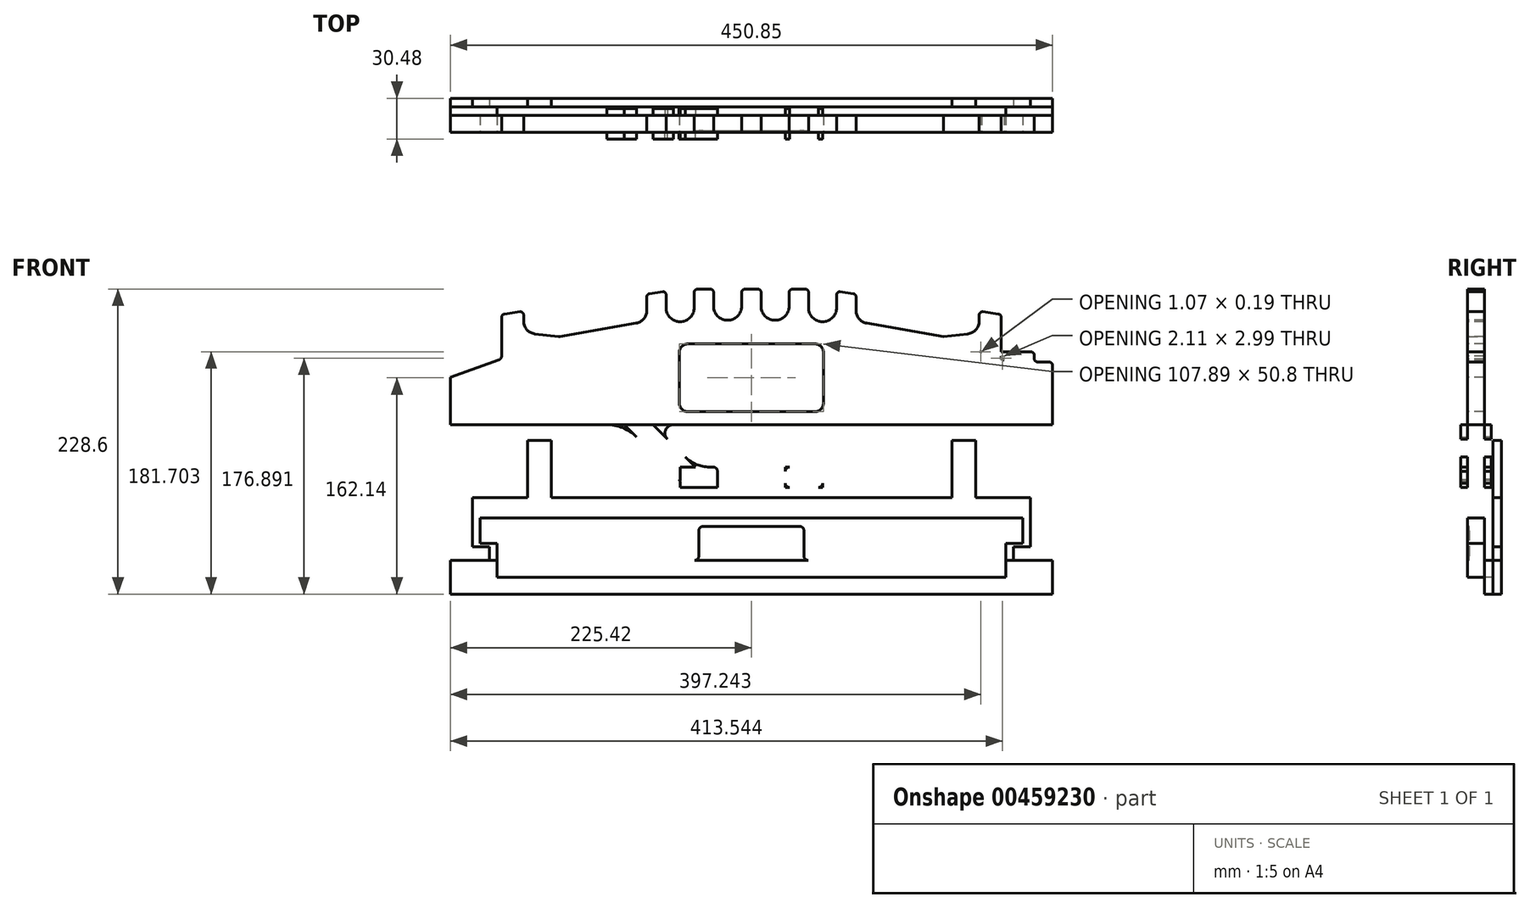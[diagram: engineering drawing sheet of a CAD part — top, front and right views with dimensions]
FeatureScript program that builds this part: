
annotation { "Feature Type Name" : "Feature", "Feature Type Description" : "" }
export const myFeature = defineFeature(function(context is Context, id is Id, definition is map)
    precondition{}
    {
        {
            var Q0;
            Q0=qCreatedBy(makeId("Front.planeOp"),FACE);
            var sketch = newSketch(context, id + "F0", { "sketchPlane" : qUnion([Q0])});
            skLineSegment(sketch, "E0", {"start": v(225.43, 44.45) * mm, "end": v(225.43, -101.6) * mm});
            skArc(sketch, "E1", {"start": v(225.42, 44.45) * mm, "mid": v(224.68, 46.25) * mm, "end": v(222.88, 47) * mm});
            skLineSegment(sketch, "E2", {"start": v(214.35, 47) * mm, "end": v(222.88, 47) * mm});
            skArc(sketch, "E3", {"start": v(211.8, 49.53) * mm, "mid": v(212.55, 47.73) * mm, "end": v(214.35, 47) * mm});
            skLineSegment(sketch, "E4", {"start": v(211.8, 52.07) * mm, "end": v(211.8, 49.53) * mm});
            skArc(sketch, "E5", {"start": v(211.8, 52.07) * mm, "mid": v(211.06, 53.87) * mm, "end": v(209.27, 54.6) * mm});
            skLineSegment(sketch, "E6", {"start": v(171.8, 54.61) * mm, "end": v(209.27, 54.61) * mm});
            skArc(sketch, "E7", {"start": v(187.07, 57.15) * mm, "mid": v(187.81, 55.35) * mm, "end": v(189.61, 54.61) * mm});
            skLineSegment(sketch, "E8", {"start": v(187.07, 80.43) * mm, "end": v(187.07, 57.15) * mm});
            skArc(sketch, "E9", {"start": v(187.07, 80.43) * mm, "mid": v(186.45, 82.1) * mm, "end": v(184.9, 82.94) * mm});
            skLineSegment(sketch, "E10", {"start": v(173.46, 84.58) * mm, "end": v(184.9, 82.94) * mm});
            skArc(sketch, "E11", {"start": v(173.46, 84.58) * mm, "mid": v(171.44, 83.98) * mm, "end": v(170.56, 82.06) * mm});
            skLineSegment(sketch, "E12", {"start": v(170.56, 77.52) * mm, "end": v(170.56, 82.06) * mm});
            skArc(sketch, "E13", {"start": v(162.11, 68.05) * mm, "mid": v(168.14, 71.17) * mm, "end": v(170.56, 77.52) * mm});
            skLineSegment(sketch, "E14", {"start": v(143.97, 65.99) * mm, "end": v(162.11, 68.05) * mm});
            skArc(sketch, "E15", {"start": v(141.12, 66.32) * mm, "mid": v(142.53, 65.99) * mm, "end": v(143.97, 65.99) * mm});
            skLineSegment(sketch, "E16", {"start": v(122.27, 73.06) * mm, "end": v(141.12, 66.32) * mm});
            skArc(sketch, "E17", {"start": v(115.95, 82.03) * mm, "mid": v(117.69, 76.54) * mm, "end": v(122.27, 73.06) * mm});
            skLineSegment(sketch, "E18", {"start": v(115.95, 90.6) * mm, "end": v(115.95, 82.03) * mm});
            skArc(sketch, "E19", {"start": v(115.95, 90.6) * mm, "mid": v(115.33, 92.26) * mm, "end": v(113.77, 93.1) * mm});
            skLineSegment(sketch, "E20", {"start": v(102.34, 94.74) * mm, "end": v(113.77, 93.1) * mm});
            skArc(sketch, "E21", {"start": v(102.34, 94.74) * mm, "mid": v(100.32, 94.14) * mm, "end": v(99.44, 92.22) * mm});
            skLineSegment(sketch, "E22", {"start": v(99.44, 85.4) * mm, "end": v(99.44, 92.22) * mm});
            skArc(sketch, "E23", {"start": v(80.4, 85.4) * mm, "mid": v(89.92, 75.87) * mm, "end": v(99.44, 85.4) * mm});
            skLineSegment(sketch, "E24", {"start": v(80.4, 95.67) * mm, "end": v(80.4, 85.4) * mm});
            skArc(sketch, "E25", {"start": v(80.4, 95.67) * mm, "mid": v(79.77, 97.34) * mm, "end": v(78.21, 98.19) * mm});
            skLineSegment(sketch, "E26", {"start": v(66.78, 99.82) * mm, "end": v(78.21, 98.19) * mm});
            skArc(sketch, "E27", {"start": v(66.78, 99.82) * mm, "mid": v(64.76, 99.22) * mm, "end": v(63.88, 97.3) * mm});
            skLineSegment(sketch, "E28", {"start": v(63.88, 87.64) * mm, "end": v(63.88, 97.3) * mm});
            skArc(sketch, "E29", {"start": v(44.83, 87.64) * mm, "mid": v(54.36, 78.12) * mm, "end": v(63.88, 87.64) * mm});
            skLineSegment(sketch, "E30", {"start": v(44.83, 99.06) * mm, "end": v(44.83, 87.64) * mm});
            skArc(sketch, "E31", {"start": v(44.83, 99.06) * mm, "mid": v(44.09, 100.86) * mm, "end": v(42.3, 101.6) * mm});
            skLineSegment(sketch, "E32", {"start": v(30.86, 101.6) * mm, "end": v(42.3, 101.6) * mm});
            skArc(sketch, "E33", {"start": v(30.86, 101.6) * mm, "mid": v(29.06, 100.86) * mm, "end": v(28.32, 99.06) * mm});
            skLineSegment(sketch, "E34", {"start": v(28.32, 88.76) * mm, "end": v(28.32, 99.06) * mm});
            skArc(sketch, "E35", {"start": v(9.27, 88.76) * mm, "mid": v(18.8, 79.24) * mm, "end": v(28.32, 88.76) * mm});
            skLineSegment(sketch, "E36", {"start": v(9.27, 99.06) * mm, "end": v(9.27, 88.76) * mm});
            skArc(sketch, "E37", {"start": v(9.27, 99.06) * mm, "mid": v(8.53, 100.86) * mm, "end": v(6.73, 101.6) * mm});
            skLineSegment(sketch, "E38", {"start": v(-4.7, 101.6) * mm, "end": v(6.73, 101.6) * mm});
            skArc(sketch, "E39", {"start": v(-4.7, 101.6) * mm, "mid": v(-6.5, 100.86) * mm, "end": v(-7.24, 99.06) * mm});
            skLineSegment(sketch, "E40", {"start": v(-7.24, 88.76) * mm, "end": v(-7.24, 99.06) * mm});
            skArc(sketch, "E41", {"start": v(-26.29, 88.76) * mm, "mid": v(-16.76, 79.24) * mm, "end": v(-7.24, 88.76) * mm});
            skLineSegment(sketch, "E42", {"start": v(-26.29, 99.06) * mm, "end": v(-26.29, 88.76) * mm});
            skArc(sketch, "E43", {"start": v(-26.29, 99.06) * mm, "mid": v(-27.03, 100.86) * mm, "end": v(-28.83, 101.6) * mm});
            skLineSegment(sketch, "E44", {"start": v(-40.26, 101.6) * mm, "end": v(-28.83, 101.6) * mm});
            skArc(sketch, "E45", {"start": v(-40.26, 101.6) * mm, "mid": v(-42.06, 100.86) * mm, "end": v(-42.8, 99.06) * mm});
            skLineSegment(sketch, "E46", {"start": v(-42.8, 87.64) * mm, "end": v(-42.8, 99.06) * mm});
            skArc(sketch, "E47", {"start": v(-61.85, 87.64) * mm, "mid": v(-52.32, 78.12) * mm, "end": v(-42.8, 87.64) * mm});
            skLineSegment(sketch, "E48", {"start": v(-61.85, 97.3) * mm, "end": v(-61.85, 87.64) * mm});
            skArc(sketch, "E49", {"start": v(-61.85, 97.3) * mm, "mid": v(-62.72, 99.23) * mm, "end": v(-64.75, 99.82) * mm});
            skLineSegment(sketch, "E50", {"start": v(-76.18, 98.19) * mm, "end": v(-64.75, 99.82) * mm});
            skArc(sketch, "E51", {"start": v(-76.18, 98.19) * mm, "mid": v(-77.74, 97.34) * mm, "end": v(-78.36, 95.67) * mm});
            skLineSegment(sketch, "E52", {"start": v(-78.36, 85.4) * mm, "end": v(-78.36, 95.67) * mm});
            skArc(sketch, "E53", {"start": v(-97.4, 85.4) * mm, "mid": v(-87.88, 75.87) * mm, "end": v(-78.36, 85.4) * mm});
            skLineSegment(sketch, "E54", {"start": v(-97.4, 92.23) * mm, "end": v(-97.4, 85.4) * mm});
            skArc(sketch, "E55", {"start": v(-97.4, 92.23) * mm, "mid": v(-98.28, 94.15) * mm, "end": v(-100.3, 94.74) * mm});
            skLineSegment(sketch, "E56", {"start": v(-111.74, 93.1) * mm, "end": v(-100.3, 94.74) * mm});
            skArc(sketch, "E57", {"start": v(-111.74, 93.1) * mm, "mid": v(-113.3, 92.26) * mm, "end": v(-113.92, 90.6) * mm});
            skLineSegment(sketch, "E58", {"start": v(-113.92, 82.03) * mm, "end": v(-113.92, 90.6) * mm});
            skArc(sketch, "E59", {"start": v(-120.24, 73.06) * mm, "mid": v(-115.66, 76.54) * mm, "end": v(-113.92, 82.03) * mm});
            skLineSegment(sketch, "E60", {"start": v(-139.09, 66.32) * mm, "end": v(-120.24, 73.06) * mm});
            skArc(sketch, "E61", {"start": v(-140.8, 65.96) * mm, "mid": v(-139.93, 66.08) * mm, "end": v(-139.09, 66.32) * mm});
            skLineSegment(sketch, "E62", {"start": v(-193.92, 62.35) * mm, "end": v(-140.8, 65.96) * mm});
            skArc(sketch, "E63", {"start": v(-204.09, 71.85) * mm, "mid": v(-201.07, 64.9) * mm, "end": v(-193.92, 62.35) * mm});
            skLineSegment(sketch, "E64", {"start": v(-204.09, 78.74) * mm, "end": v(-204.09, 71.85) * mm});
            skArc(sketch, "E65", {"start": v(-204.09, 78.74) * mm, "mid": v(-204.83, 80.54) * mm, "end": v(-206.63, 81.28) * mm});
            skLineSegment(sketch, "E66", {"start": v(-222.89, 81.28) * mm, "end": v(-206.63, 81.28) * mm});
            skArc(sketch, "E67", {"start": v(-222.89, 81.28) * mm, "mid": v(-224.68, 80.54) * mm, "end": v(-225.43, 78.74) * mm});
            skLineSegment(sketch, "E68", {"start": v(-225.43, -101.6) * mm, "end": v(-225.43, 78.74) * mm});
            skLineSegment(sketch, "E69", {"start": v(-193.68, -101.6) * mm, "end": v(-225.43, -101.6) * mm});
            skLineSegment(sketch, "E70", {"start": v(-193.68, -88.9) * mm, "end": v(-193.68, -101.6) * mm});
            skLineSegment(sketch, "E71", {"start": v(-206.38, -88.9) * mm, "end": v(-193.68, -88.9) * mm});
            skLineSegment(sketch, "E72", {"start": v(-206.38, -57.15) * mm, "end": v(-206.38, -88.9) * mm});
            skLineSegment(sketch, "E73", {"start": v(-165.35, -57.15) * mm, "end": v(-206.38, -57.15) * mm});
            skLineSegment(sketch, "E74", {"start": v(-165.35, -14.48) * mm, "end": v(-165.35, -57.15) * mm});
            skLineSegment(sketch, "E75", {"start": v(-152.4, -14.48) * mm, "end": v(-165.35, -14.48) * mm});
            skLineSegment(sketch, "E76", {"start": v(-152.4, -57.15) * mm, "end": v(-152.4, -14.48) * mm});
            skLineSegment(sketch, "E77", {"start": v(152.4, -57.15) * mm, "end": v(-152.4, -57.15) * mm});
            skLineSegment(sketch, "E78", {"start": v(152.4, -14.48) * mm, "end": v(152.4, -57.15) * mm});
            skLineSegment(sketch, "E79", {"start": v(165.35, -14.48) * mm, "end": v(152.4, -14.48) * mm});
            skLineSegment(sketch, "E80", {"start": v(165.35, -57.15) * mm, "end": v(165.35, -14.48) * mm});
            skLineSegment(sketch, "E81", {"start": v(206.38, -57.15) * mm, "end": v(165.35, -57.15) * mm});
            skLineSegment(sketch, "E82", {"start": v(206.38, -88.9) * mm, "end": v(206.38, -57.15) * mm});
            skLineSegment(sketch, "E83", {"start": v(193.68, -88.9) * mm, "end": v(206.38, -88.9) * mm});
            skLineSegment(sketch, "E84", {"start": v(193.68, -101.6) * mm, "end": v(193.68, -88.9) * mm});
            skLineSegment(sketch, "E85", {"start": v(225.43, -101.6) * mm, "end": v(193.68, -101.6) * mm});
            skLineSegment(sketch, "E86", {"start": v(47.6, 9.74) * mm, "end": v(-47.6, 9.74) * mm});
            skArc(sketch, "E87", {"start": v(-53.95, 16.1) * mm, "mid": v(-52.09, 11.6) * mm, "end": v(-47.6, 9.74) * mm});
            skLineSegment(sketch, "E88", {"start": v(-53.95, 16.1) * mm, "end": v(-53.95, 54.2) * mm});
            skArc(sketch, "E89", {"start": v(-47.6, 60.54) * mm, "mid": v(-52.09, 58.68) * mm, "end": v(-53.95, 54.2) * mm});
            skLineSegment(sketch, "E90", {"start": v(-47.6, 60.54) * mm, "end": v(47.6, 60.54) * mm});
            skArc(sketch, "E91", {"start": v(53.95, 54.2) * mm, "mid": v(52.09, 58.68) * mm, "end": v(47.6, 60.54) * mm});
            skLineSegment(sketch, "E92", {"start": v(53.95, 54.2) * mm, "end": v(53.95, 16.1) * mm});
            skArc(sketch, "E93", {"start": v(47.6, 9.74) * mm, "mid": v(52.09, 11.6) * mm, "end": v(53.95, 16.1) * mm});
            skLineSegment(sketch, "E94", {"start": v(225.43, -101.6) * mm, "end": v(-225.43, -101.6) * mm, "construction": true});
            skLineSegment(sketch, "E95", {"start": v(-225.43, -101.6) * mm, "end": v(-225.43, 0) * mm, "construction": true});
            skLineSegment(sketch, "E96", {"start": v(-225.43, 0) * mm, "end": v(225.43, 0) * mm});
            skLineSegment(sketch, "E97", {"start": v(225.43, 0) * mm, "end": v(225.43, -101.6) * mm, "construction": true});
            skLineSegment(sketch, "E98", {"start": v(0, -604.73) * mm, "end": v(0, 474.28) * mm, "construction": true});
            skArc(sketch, "E99.MirrorCS", {"start": v(-44.83, 99.06) * mm, "mid": v(-44.09, 100.86) * mm, "end": v(-42.3, 101.6) * mm});
            skArc(sketch, "E100.MirrorCS", {"start": v(111.74, 93.1) * mm, "mid": v(113.3, 92.26) * mm, "end": v(113.92, 90.6) * mm});
            skLineSegment(sketch, "E101.MirrorCS", {"start": v(7.24, 88.76) * mm, "end": v(7.24, 99.06) * mm});
            skLineSegment(sketch, "E102.MirrorCS", {"start": v(-30.86, 101.6) * mm, "end": v(-42.3, 101.6) * mm});
            skArc(sketch, "E103.MirrorCS", {"start": v(4.7, 101.6) * mm, "mid": v(6.5, 100.86) * mm, "end": v(7.24, 99.06) * mm});
            skArc(sketch, "E104.MirrorCS", {"start": v(-211.8, 52.07) * mm, "mid": v(-211.06, 53.87) * mm, "end": v(-209.27, 54.6) * mm});
            skLineSegment(sketch, "E105.MirrorCS", {"start": v(-211.8, 52.07) * mm, "end": v(-211.8, 49.53) * mm});
            skArc(sketch, "E106.MirrorCS", {"start": v(-211.8, 49.53) * mm, "mid": v(-212.55, 47.73) * mm, "end": v(-214.35, 47) * mm});
            skLineSegment(sketch, "E107.MirrorCS", {"start": v(113.92, 82.03) * mm, "end": v(113.92, 90.6) * mm});
            skLineSegment(sketch, "E108.MirrorCS", {"start": v(-28.32, 88.76) * mm, "end": v(-28.32, 99.06) * mm});
            skLineSegment(sketch, "E109.MirrorCS", {"start": v(-115.95, 90.6) * mm, "end": v(-115.95, 82.03) * mm});
            skLineSegment(sketch, "E110.MirrorCS", {"start": v(4.7, 101.6) * mm, "end": v(-6.73, 101.6) * mm});
            skArc(sketch, "E111.MirrorCS", {"start": v(-30.86, 101.6) * mm, "mid": v(-29.06, 100.86) * mm, "end": v(-28.32, 99.06) * mm});
            skArc(sketch, "E112.MirrorCS", {"start": v(-9.27, 99.06) * mm, "mid": v(-8.53, 100.86) * mm, "end": v(-6.73, 101.6) * mm});
            skLineSegment(sketch, "E113.MirrorCS", {"start": v(40.26, 101.6) * mm, "end": v(28.83, 101.6) * mm});
            skArc(sketch, "E114.MirrorCS", {"start": v(40.26, 101.6) * mm, "mid": v(42.06, 100.86) * mm, "end": v(42.8, 99.06) * mm});
            skLineSegment(sketch, "E115.MirrorCS", {"start": v(-9.27, 99.06) * mm, "end": v(-9.27, 88.76) * mm});
            skArc(sketch, "E116.MirrorCS", {"start": v(140.8, 65.96) * mm, "mid": v(139.93, 66.08) * mm, "end": v(139.09, 66.32) * mm});
            skLineSegment(sketch, "E117.MirrorCS", {"start": v(-102.34, 94.74) * mm, "end": v(-113.77, 93.1) * mm});
            skArc(sketch, "E118.MirrorCS", {"start": v(26.29, 99.06) * mm, "mid": v(27.03, 100.86) * mm, "end": v(28.83, 101.6) * mm});
            skArc(sketch, "E119.MirrorCS", {"start": v(76.18, 98.19) * mm, "mid": v(77.74, 97.34) * mm, "end": v(78.36, 95.67) * mm});
            skArc(sketch, "E120.MirrorCS", {"start": v(-115.95, 90.6) * mm, "mid": v(-115.33, 92.26) * mm, "end": v(-113.77, 93.1) * mm});
            skLineSegment(sketch, "E121.MirrorCS", {"start": v(26.29, 99.06) * mm, "end": v(26.29, 88.76) * mm});
            skLineSegment(sketch, "E122.MirrorCS", {"start": v(76.18, 98.19) * mm, "end": v(64.75, 99.82) * mm});
            skLineSegment(sketch, "E123.MirrorCS", {"start": v(97.4, 92.23) * mm, "end": v(97.4, 85.4) * mm});
            skLineSegment(sketch, "E124.MirrorCS", {"start": v(-99.44, 85.4) * mm, "end": v(-99.44, 92.22) * mm});
            skArc(sketch, "E125.MirrorCS", {"start": v(61.85, 97.3) * mm, "mid": v(62.72, 99.23) * mm, "end": v(64.75, 99.82) * mm});
            skArc(sketch, "E126.MirrorCS", {"start": v(204.09, 78.74) * mm, "mid": v(204.83, 80.54) * mm, "end": v(206.63, 81.28) * mm});
            skLineSegment(sketch, "E127.MirrorCS", {"start": v(42.8, 87.64) * mm, "end": v(42.8, 99.06) * mm});
            skArc(sketch, "E128.MirrorCS", {"start": v(-102.34, 94.74) * mm, "mid": v(-100.32, 94.14) * mm, "end": v(-99.44, 92.22) * mm});
            skLineSegment(sketch, "E129.MirrorCS", {"start": v(-63.88, 87.64) * mm, "end": v(-63.88, 97.3) * mm});
            skLineSegment(sketch, "E130.MirrorCS", {"start": v(111.74, 93.1) * mm, "end": v(100.3, 94.74) * mm});
            skLineSegment(sketch, "E131.MirrorCS", {"start": v(61.85, 97.3) * mm, "end": v(61.85, 87.64) * mm});
            skLineSegment(sketch, "E132.MirrorCS", {"start": v(204.09, 78.74) * mm, "end": v(204.09, 71.85) * mm});
            skLineSegment(sketch, "E133.MirrorCS", {"start": v(78.36, 85.4) * mm, "end": v(78.36, 95.67) * mm});
            skArc(sketch, "E134.MirrorCS", {"start": v(-66.78, 99.82) * mm, "mid": v(-64.76, 99.22) * mm, "end": v(-63.88, 97.3) * mm});
            skArc(sketch, "E135.MirrorCS", {"start": v(97.4, 92.23) * mm, "mid": v(98.28, 94.15) * mm, "end": v(100.3, 94.74) * mm});
            skLineSegment(sketch, "E136.MirrorCS", {"start": v(-170.56, 77.52) * mm, "end": v(-170.56, 82.06) * mm});
            skArc(sketch, "E137.MirrorCS", {"start": v(-173.46, 84.58) * mm, "mid": v(-171.44, 83.98) * mm, "end": v(-170.56, 82.06) * mm});
            skLineSegment(sketch, "E138.MirrorCS", {"start": v(-173.46, 84.58) * mm, "end": v(-184.9, 82.94) * mm});
            skArc(sketch, "E139.MirrorCS", {"start": v(-187.07, 80.43) * mm, "mid": v(-186.45, 82.1) * mm, "end": v(-184.9, 82.94) * mm});
            skLineSegment(sketch, "E140.MirrorCS", {"start": v(-187.07, 80.43) * mm, "end": v(-187.07, 57.15) * mm});
            skArc(sketch, "E141.MirrorCS", {"start": v(-187.07, 57.15) * mm, "mid": v(-187.81, 55.35) * mm, "end": v(-189.61, 54.61) * mm});
            skLineSegment(sketch, "E142.MirrorCS", {"start": v(-171.8, 54.61) * mm, "end": v(-209.27, 54.61) * mm});
            skLineSegment(sketch, "E143.MirrorCS", {"start": v(-66.78, 99.82) * mm, "end": v(-78.21, 98.19) * mm});
            skLineSegment(sketch, "E144.MirrorCS", {"start": v(222.89, 81.28) * mm, "end": v(206.63, 81.28) * mm});
            skArc(sketch, "E145.MirrorCS", {"start": v(-162.11, 68.05) * mm, "mid": v(-168.14, 71.17) * mm, "end": v(-170.56, 77.52) * mm});
            skLineSegment(sketch, "E146.MirrorCS", {"start": v(193.68, -88.9) * mm, "end": v(193.68, -101.6) * mm});
            skArc(sketch, "E147.MirrorCS", {"start": v(204.09, 71.85) * mm, "mid": v(201.07, 64.9) * mm, "end": v(193.92, 62.35) * mm});
            skLineSegment(sketch, "E148.MirrorCS", {"start": v(-165.35, -14.48) * mm, "end": v(-152.4, -14.48) * mm});
            skArc(sketch, "E149.MirrorCS", {"start": v(47.6, 60.54) * mm, "mid": v(52.09, 58.68) * mm, "end": v(53.95, 54.2) * mm});
            skArc(sketch, "E150.MirrorCS", {"start": v(-80.4, 95.67) * mm, "mid": v(-79.77, 97.34) * mm, "end": v(-78.21, 98.19) * mm});
            skArc(sketch, "E151.MirrorCS", {"start": v(26.29, 88.76) * mm, "mid": v(16.76, 79.24) * mm, "end": v(7.24, 88.76) * mm});
            skLineSegment(sketch, "E152.MirrorCS", {"start": v(-44.83, 99.06) * mm, "end": v(-44.83, 87.64) * mm});
            skArc(sketch, "E153.MirrorCS", {"start": v(97.4, 85.4) * mm, "mid": v(87.88, 75.87) * mm, "end": v(78.36, 85.4) * mm});
            skArc(sketch, "E154.MirrorCS", {"start": v(-115.95, 82.03) * mm, "mid": v(-117.69, 76.54) * mm, "end": v(-122.27, 73.06) * mm});
            skLineSegment(sketch, "E155.MirrorCS", {"start": v(-80.4, 95.67) * mm, "end": v(-80.4, 85.4) * mm});
            skLineSegment(sketch, "E156.MirrorCS", {"start": v(139.09, 66.32) * mm, "end": v(120.24, 73.06) * mm});
            skArc(sketch, "E157.MirrorCS", {"start": v(-47.6, 9.74) * mm, "mid": v(-52.09, 11.6) * mm, "end": v(-53.95, 16.1) * mm});
            skLineSegment(sketch, "E158.MirrorCS", {"start": v(-122.27, 73.06) * mm, "end": v(-141.12, 66.32) * mm});
            skLineSegment(sketch, "E159.MirrorCS", {"start": v(-193.68, -101.6) * mm, "end": v(-193.68, -88.9) * mm});
            skLineSegment(sketch, "E160.MirrorCS", {"start": v(206.38, -88.9) * mm, "end": v(193.68, -88.9) * mm});
            skArc(sketch, "E161.MirrorCS", {"start": v(53.95, 16.1) * mm, "mid": v(52.09, 11.6) * mm, "end": v(47.6, 9.74) * mm});
            skArc(sketch, "E162.MirrorCS", {"start": v(-80.4, 85.4) * mm, "mid": v(-89.92, 75.87) * mm, "end": v(-99.44, 85.4) * mm});
            skLineSegment(sketch, "E163.MirrorCS", {"start": v(152.4, -14.48) * mm, "end": v(165.35, -14.48) * mm});
            skArc(sketch, "E164.MirrorCS", {"start": v(-53.95, 54.2) * mm, "mid": v(-52.09, 58.68) * mm, "end": v(-47.6, 60.54) * mm});
            skArc(sketch, "E165.MirrorCS", {"start": v(120.24, 73.06) * mm, "mid": v(115.66, 76.54) * mm, "end": v(113.92, 82.03) * mm});
            skLineSegment(sketch, "E166.MirrorCS", {"start": v(-214.35, 47) * mm, "end": v(-222.88, 47) * mm});
            skArc(sketch, "E167.MirrorCS", {"start": v(-225.42, 44.45) * mm, "mid": v(-224.68, 46.25) * mm, "end": v(-222.88, 47) * mm});
            skLineSegment(sketch, "E168.MirrorCS", {"start": v(-143.97, 65.99) * mm, "end": v(-162.11, 68.05) * mm});
            skArc(sketch, "E169.MirrorCS", {"start": v(-9.27, 88.76) * mm, "mid": v(-18.8, 79.24) * mm, "end": v(-28.32, 88.76) * mm});
            skArc(sketch, "E170.MirrorCS", {"start": v(222.89, 81.28) * mm, "mid": v(224.68, 80.54) * mm, "end": v(225.43, 78.74) * mm});
            skLineSegment(sketch, "E171.MirrorCS", {"start": v(-193.68, -88.9) * mm, "end": v(-206.38, -88.9) * mm});
            skLineSegment(sketch, "E172.MirrorCS", {"start": v(193.68, -101.6) * mm, "end": v(225.43, -101.6) * mm});
            skLineSegment(sketch, "E173.MirrorCS", {"start": v(-225.43, -101.6) * mm, "end": v(-193.68, -101.6) * mm});
            skLineSegment(sketch, "E174.MirrorCS", {"start": v(-206.38, -88.9) * mm, "end": v(-206.38, -57.15) * mm});
            skLineSegment(sketch, "E175.MirrorCS", {"start": v(225.43, -101.6) * mm, "end": v(225.43, 0) * mm, "construction": true});
            skArc(sketch, "E176.MirrorCS", {"start": v(61.85, 87.64) * mm, "mid": v(52.32, 78.12) * mm, "end": v(42.8, 87.64) * mm});
            skLineSegment(sketch, "E177.MirrorCS", {"start": v(-47.6, 9.74) * mm, "end": v(47.6, 9.74) * mm});
            skLineSegment(sketch, "E178.MirrorCS", {"start": v(165.35, -57.15) * mm, "end": v(206.38, -57.15) * mm});
            skLineSegment(sketch, "E179.MirrorCS", {"start": v(-225.43, 0) * mm, "end": v(-225.43, -101.6) * mm, "construction": true});
            skLineSegment(sketch, "E180.MirrorCS", {"start": v(-206.38, -57.15) * mm, "end": v(-165.35, -57.15) * mm});
            skLineSegment(sketch, "E181.MirrorCS", {"start": v(-225.43, -101.6) * mm, "end": v(225.43, -101.6) * mm, "construction": true});
            skLineSegment(sketch, "E182.MirrorCS", {"start": v(193.92, 62.35) * mm, "end": v(140.8, 65.96) * mm});
            skLineSegment(sketch, "E183.MirrorCS", {"start": v(-152.4, -14.48) * mm, "end": v(-152.4, -57.15) * mm});
            skLineSegment(sketch, "E184.MirrorCS", {"start": v(206.38, -57.15) * mm, "end": v(206.38, -88.9) * mm});
            skLineSegment(sketch, "E185.MirrorCS", {"start": v(53.95, 16.1) * mm, "end": v(53.95, 54.2) * mm});
            skLineSegment(sketch, "E186.MirrorCS", {"start": v(152.4, -57.15) * mm, "end": v(152.4, -14.48) * mm});
            skLineSegment(sketch, "E187.MirrorCS", {"start": v(-53.95, 54.2) * mm, "end": v(-53.95, 16.1) * mm});
            skLineSegment(sketch, "E188.MirrorCS", {"start": v(-165.35, -57.15) * mm, "end": v(-165.35, -14.48) * mm});
            skArc(sketch, "E189.MirrorCS", {"start": v(-44.83, 87.64) * mm, "mid": v(-54.36, 78.12) * mm, "end": v(-63.88, 87.64) * mm});
            skLineSegment(sketch, "E190.MirrorCS", {"start": v(-152.4, -57.15) * mm, "end": v(152.4, -57.15) * mm});
            skLineSegment(sketch, "E191.MirrorCS", {"start": v(225.43, -101.6) * mm, "end": v(225.43, 78.74) * mm});
            skLineSegment(sketch, "E192.MirrorCS", {"start": v(225.43, 0) * mm, "end": v(-225.43, 0) * mm});
            skLineSegment(sketch, "E193.MirrorCS", {"start": v(-225.43, 44.45) * mm, "end": v(-225.43, -101.6) * mm});
            skLineSegment(sketch, "E194.MirrorCS", {"start": v(165.35, -14.48) * mm, "end": v(165.35, -57.15) * mm});
            skLineSegment(sketch, "E195.MirrorCS", {"start": v(47.6, 60.54) * mm, "end": v(-47.6, 60.54) * mm});
            skLineSegment(sketch, "E196", {"start": v(-139.09, 66.32) * mm, "end": v(-229.43, 34) * mm});
            skLineSegment(sketch, "E197.MirrorCS", {"start": v(139.09, 66.32) * mm, "end": v(229.43, 34) * mm});
            skPoint(sketch, "E198.orphan", {"position": v(-189.61, 54.61) * mm});
            skPoint(sketch, "E199.orphan", {"position": v(189.61, 54.61) * mm});
            skArc(sketch, "E200", {"start": v(-172.36, 54.61) * mm, "mid": v(-171.81, 54.66) * mm, "end": v(-171.29, 54.8) * mm});
            skArc(sketch, "E201.MirrorCS", {"start": v(172.36, 54.61) * mm, "mid": v(171.81, 54.66) * mm, "end": v(171.29, 54.8) * mm});
            skPoint(sketch, "E202.orphan", {"position": v(-187.07, 80.43) * mm});
            skLineSegment(sketch, "E203", {"start": v(-187.07, 57.15) * mm, "end": v(-187.07, 49.15) * mm});
            skArc(sketch, "E204", {"start": v(-189.18, 48.4) * mm, "mid": v(-187.65, 49.56) * mm, "end": v(-187.07, 51.39) * mm});
            skLineSegment(sketch, "E205.MirrorCS", {"start": v(187.07, 57.15) * mm, "end": v(187.07, 49.15) * mm});
            skArc(sketch, "E206.MirrorCS", {"start": v(189.18, 48.4) * mm, "mid": v(187.65, 49.56) * mm, "end": v(187.07, 51.39) * mm});
            skLineSegment(sketch, "E207", {"start": v(-143.97, 65.99) * mm, "end": v(-86.25, 76.01) * mm});
            skArc(sketch, "E208", {"start": v(-144.43, 66.04) * mm, "mid": v(-143.98, 66.02) * mm, "end": v(-143.53, 66.06) * mm});
            skArc(sketch, "E209.MirrorCS", {"start": v(144.43, 66.04) * mm, "mid": v(143.98, 66.02) * mm, "end": v(143.53, 66.06) * mm});
            skLineSegment(sketch, "E210.MirrorCS", {"start": v(143.97, 65.99) * mm, "end": v(86.25, 76.01) * mm});
            skArc(sketch, "E211", {"start": v(-63.88, 87.64) * mm, "mid": v(-53.34, 77.1) * mm, "end": v(-42.8, 87.64) * mm});
            skArc(sketch, "E212", {"start": v(-63.88, 97.3) * mm, "mid": v(-64.67, 99.03) * mm, "end": v(-66.5, 99.57) * mm});
            skArc(sketch, "E213.MirrorCS", {"start": v(63.88, 97.3) * mm, "mid": v(64.67, 99.03) * mm, "end": v(66.5, 99.57) * mm});
            skArc(sketch, "E214.MirrorCS", {"start": v(63.88, 87.64) * mm, "mid": v(53.34, 77.1) * mm, "end": v(42.8, 87.64) * mm});
            skArc(sketch, "E215", {"start": v(-28.32, 88.76) * mm, "mid": v(-17.78, 78.22) * mm, "end": v(-7.24, 88.76) * mm});
            skArc(sketch, "E216.MirrorCS", {"start": v(28.32, 88.76) * mm, "mid": v(17.78, 78.22) * mm, "end": v(7.24, 88.76) * mm});
            skSolve(sketch);
        }
        {
            var Q0;
            Q0=makeQuery(id+"F0.imprint","IMPRINT",FACE,{"disambiguationData":[TD([[makeQuery(id+"F0.imprint","IMPRINT",EDGE,{"derivedFrom":sQuery(id+"F0.wireOp",EDGE,"E146.MirrorCS")}),1.0]])]});
            var Q1;
            {var subQ3=sQuery(id+"F0.wireOp",EDGE,"E200");Q1=makeQuery(id+"F0.imprint","IMPRINT",FACE,{"disambiguationData":[TD([[makeQuery(id+"F0.imprint","IMPRINT",EDGE,{"derivedFrom":subQ3}),-1.0]])]});}
            var Q2;
            {var subQ3=sQuery(id+"F0.wireOp",EDGE,"E201.MirrorCS");Q2=makeQuery(id+"F0.imprint","IMPRINT",FACE,{"disambiguationData":[TD([[makeQuery(id+"F0.imprint","IMPRINT",EDGE,{"derivedFrom":subQ3}),1.0]])]});}
            var Q3;
            {var subQ8=sQuery(id+"F0.wireOp",EDGE,"E61");Q3=makeQuery(id+"F0.imprint","IMPRINT",FACE,{"disambiguationData":[TD([[makeQuery(id+"F0.imprint","IMPRINT",EDGE,{"derivedFrom":subQ8}),-1.0]])]});}
            var Q4;
            {var subQ2=sQuery(id+"F0.wireOp",EDGE,"E142.MirrorCS");var subQ4=sQuery(id+"F0.wireOp",EDGE,"E196");var subQ5=makeQuery(id+"F0.imprint","INTERSECT",VERTEX,{"derivedFrom":[subQ2,subQ4]});Q4=makeQuery(id+"F0.imprint","IMPRINT",FACE,{"disambiguationData":[TD([[makeQuery(id+"F0.imprint","IMPRINT",EDGE,{"disambiguationData":[TD([[subQ5,-1.0]])],"derivedFrom":subQ2}),1.0]])]});}
            var Q5;
            {var subQ3=sQuery(id+"F0.wireOp",EDGE,"E204");Q5=makeQuery(id+"F0.imprint","IMPRINT",FACE,{"disambiguationData":[TD([[makeQuery(id+"F0.imprint","IMPRINT",EDGE,{"derivedFrom":subQ3}),-1.0]])]});}
            var Q6;
            {var subQ5=sQuery(id+"F0.wireOp",EDGE,"E9");Q6=makeQuery(id+"F0.imprint","IMPRINT",FACE,{"disambiguationData":[TD([[makeQuery(id+"F0.imprint","IMPRINT",EDGE,{"derivedFrom":subQ5}),1.0]])]});}
            var Q7;
            {var subQ0=sQuery(id+"F0.wireOp",EDGE,"E116.MirrorCS");Q7=makeQuery(id+"F0.imprint","IMPRINT",FACE,{"disambiguationData":[TD([[makeQuery(id+"F0.imprint","IMPRINT",EDGE,{"derivedFrom":subQ0}),1.0]])]});}
            var Q8;
            {var subQ2=sQuery(id+"F0.wireOp",EDGE,"E6");var subQ4=sQuery(id+"F0.wireOp",EDGE,"E197.MirrorCS");var subQ5=makeQuery(id+"F0.imprint","INTERSECT",VERTEX,{"derivedFrom":[subQ2,subQ4]});Q8=makeQuery(id+"F0.imprint","IMPRINT",FACE,{"disambiguationData":[TD([[makeQuery(id+"F0.imprint","IMPRINT",EDGE,{"disambiguationData":[TD([[subQ5,-1.0]])],"derivedFrom":subQ2}),-1.0]])]});}
            var Q9;
            {var subQ3=sQuery(id+"F0.wireOp",EDGE,"E206.MirrorCS");Q9=makeQuery(id+"F0.imprint","IMPRINT",FACE,{"disambiguationData":[TD([[makeQuery(id+"F0.imprint","IMPRINT",EDGE,{"derivedFrom":subQ3}),1.0]])]});}
            var Q10;
            {var subQ43=sQuery(id+"F0.wireOp",EDGE,"E28");Q10=makeQuery(id+"F0.imprint","IMPRINT",FACE,{"disambiguationData":[TD([[makeQuery(id+"F0.imprint","IMPRINT",EDGE,{"derivedFrom":subQ43}),-1.0]])]});}
            var Q11;
            {var subQ6=sQuery(id+"F0.wireOp",EDGE,"E61");Q11=makeQuery(id+"F0.imprint","IMPRINT",FACE,{"disambiguationData":[TD([[makeQuery(id+"F0.imprint","IMPRINT",EDGE,{"derivedFrom":subQ6}),1.0]])]});}
            var Q12;
            {var subQ3=sQuery(id+"F0.wireOp",EDGE,"E208");Q12=makeQuery(id+"F0.imprint","IMPRINT",FACE,{"disambiguationData":[TD([[makeQuery(id+"F0.imprint","IMPRINT",EDGE,{"derivedFrom":subQ3}),-1.0]])]});}
            var Q13;
            {var subQ0=sQuery(id+"F0.wireOp",EDGE,"E15");Q13=makeQuery(id+"F0.imprint","IMPRINT",FACE,{"disambiguationData":[TD([[makeQuery(id+"F0.imprint","IMPRINT",EDGE,{"derivedFrom":subQ0}),1.0]])]});}
            var Q14;
            {var subQ3=sQuery(id+"F0.wireOp",EDGE,"E209.MirrorCS");Q14=makeQuery(id+"F0.imprint","IMPRINT",FACE,{"disambiguationData":[TD([[makeQuery(id+"F0.imprint","IMPRINT",EDGE,{"derivedFrom":subQ3}),1.0]])]});}
            extrude(context, id + "F1", {"entities" : qUnion([Q0, Q1, Q2, Q3, Q4, Q5, Q6, Q7, Q8, Q9, Q10, Q11, Q12, Q13, Q14]), "oppositeDirection" : true, "depth" : 12.7 * mm});
        }
        {
            var Q0;
            Q0=makeQuery(id+"F1.opExtrude","CAP_FACE",FACE,{"disambiguationData":[OSD([sQuery(id+"F0.wireOp",EDGE,"f3b8bc04-095d-494a-bcce-8306202adf07"),sQuery(id+"F0.wireOp",EDGE,"08e92012-2e21-4d94-9f0a-c8e57075e395"),sQuery(id+"F0.wireOp",EDGE,"122fa739-26d1-4298-ae19-82ac91bd4e23"),sQuery(id+"F0.wireOp",EDGE,"d5e32c5b-27bd-42dd-9b3f-d947ba78b5c6"),sQuery(id+"F0.wireOp",EDGE,"E0"),sQuery(id+"F0.wireOp",EDGE,"E1"),sQuery(id+"F0.wireOp",EDGE,"E2"),sQuery(id+"F0.wireOp",EDGE,"E3"),sQuery(id+"F0.wireOp",EDGE,"E4"),sQuery(id+"F0.wireOp",EDGE,"E5"),sQuery(id+"F0.wireOp",EDGE,"E6"),sQuery(id+"F0.wireOp",EDGE,"E7"),sQuery(id+"F0.wireOp",EDGE,"E8"),sQuery(id+"F0.wireOp",EDGE,"E9"),sQuery(id+"F0.wireOp",EDGE,"E10"),sQuery(id+"F0.wireOp",EDGE,"E11"),sQuery(id+"F0.wireOp",EDGE,"E12"),sQuery(id+"F0.wireOp",EDGE,"E13"),sQuery(id+"F0.wireOp",EDGE,"E14"),sQuery(id+"F0.wireOp",EDGE,"E15"),sQuery(id+"F0.wireOp",EDGE,"E16"),sQuery(id+"F0.wireOp",EDGE,"E17"),sQuery(id+"F0.wireOp",EDGE,"E18"),sQuery(id+"F0.wireOp",EDGE,"E19"),sQuery(id+"F0.wireOp",EDGE,"E20"),sQuery(id+"F0.wireOp",EDGE,"E21"),sQuery(id+"F0.wireOp",EDGE,"E22"),sQuery(id+"F0.wireOp",EDGE,"E23"),sQuery(id+"F0.wireOp",EDGE,"E24"),sQuery(id+"F0.wireOp",EDGE,"E25"),sQuery(id+"F0.wireOp",EDGE,"E26"),sQuery(id+"F0.wireOp",EDGE,"E27"),sQuery(id+"F0.wireOp",EDGE,"E28"),sQuery(id+"F0.wireOp",EDGE,"E29"),sQuery(id+"F0.wireOp",EDGE,"E30"),sQuery(id+"F0.wireOp",EDGE,"E31"),sQuery(id+"F0.wireOp",EDGE,"E32"),sQuery(id+"F0.wireOp",EDGE,"E33"),sQuery(id+"F0.wireOp",EDGE,"E34"),sQuery(id+"F0.wireOp",EDGE,"E35"),sQuery(id+"F0.wireOp",EDGE,"E36"),sQuery(id+"F0.wireOp",EDGE,"E37"),sQuery(id+"F0.wireOp",EDGE,"E38"),sQuery(id+"F0.wireOp",EDGE,"E39"),sQuery(id+"F0.wireOp",EDGE,"E40"),sQuery(id+"F0.wireOp",EDGE,"E41"),sQuery(id+"F0.wireOp",EDGE,"E42"),sQuery(id+"F0.wireOp",EDGE,"E43"),sQuery(id+"F0.wireOp",EDGE,"E44"),sQuery(id+"F0.wireOp",EDGE,"E45"),sQuery(id+"F0.wireOp",EDGE,"E46"),sQuery(id+"F0.wireOp",EDGE,"E47"),sQuery(id+"F0.wireOp",EDGE,"E48"),sQuery(id+"F0.wireOp",EDGE,"E49"),sQuery(id+"F0.wireOp",EDGE,"E50"),sQuery(id+"F0.wireOp",EDGE,"E51"),sQuery(id+"F0.wireOp",EDGE,"E52"),sQuery(id+"F0.wireOp",EDGE,"E53"),sQuery(id+"F0.wireOp",EDGE,"E54"),sQuery(id+"F0.wireOp",EDGE,"E55"),sQuery(id+"F0.wireOp",EDGE,"E56"),sQuery(id+"F0.wireOp",EDGE,"E57"),sQuery(id+"F0.wireOp",EDGE,"E58"),sQuery(id+"F0.wireOp",EDGE,"E59"),sQuery(id+"F0.wireOp",EDGE,"E60"),sQuery(id+"F0.wireOp",EDGE,"E61"),sQuery(id+"F0.wireOp",EDGE,"E62"),sQuery(id+"F0.wireOp",EDGE,"E63"),sQuery(id+"F0.wireOp",EDGE,"E64"),sQuery(id+"F0.wireOp",EDGE,"E65"),sQuery(id+"F0.wireOp",EDGE,"E66"),sQuery(id+"F0.wireOp",EDGE,"E67"),sQuery(id+"F0.wireOp",EDGE,"E68"),sQuery(id+"F0.wireOp",EDGE,"E69"),sQuery(id+"F0.wireOp",EDGE,"E70"),sQuery(id+"F0.wireOp",EDGE,"E71"),sQuery(id+"F0.wireOp",EDGE,"E72"),sQuery(id+"F0.wireOp",EDGE,"E73"),sQuery(id+"F0.wireOp",EDGE,"E74"),sQuery(id+"F0.wireOp",EDGE,"E75"),sQuery(id+"F0.wireOp",EDGE,"E76"),sQuery(id+"F0.wireOp",EDGE,"E77"),sQuery(id+"F0.wireOp",EDGE,"E78"),sQuery(id+"F0.wireOp",EDGE,"E79"),sQuery(id+"F0.wireOp",EDGE,"E80"),sQuery(id+"F0.wireOp",EDGE,"E81"),sQuery(id+"F0.wireOp",EDGE,"E82"),sQuery(id+"F0.wireOp",EDGE,"E83"),sQuery(id+"F0.wireOp",EDGE,"E84"),sQuery(id+"F0.wireOp",EDGE,"E85"),sQuery(id+"F0.wireOp",EDGE,"2d70706d-4c91-45b7-b293-bf747273fc1e"),sQuery(id+"F0.wireOp",EDGE,"f606c3c6-6e26-49ba-bb4a-ffbf22b89f78"),sQuery(id+"F0.wireOp",EDGE,"6ded5a20-7a3f-46e3-8459-1bb58dbc2f72"),sQuery(id+"F0.wireOp",EDGE,"099ca5a8-81e7-49d1-b38d-3a86f93f5891"),sQuery(id+"F0.wireOp",EDGE,"E86"),sQuery(id+"F0.wireOp",EDGE,"E87"),sQuery(id+"F0.wireOp",EDGE,"E88"),sQuery(id+"F0.wireOp",EDGE,"E89"),sQuery(id+"F0.wireOp",EDGE,"E90"),sQuery(id+"F0.wireOp",EDGE,"E91"),sQuery(id+"F0.wireOp",EDGE,"E92"),sQuery(id+"F0.wireOp",EDGE,"E93")])],"isStart":true});
            cPlane(context, id + "F2", {"entities" : qUnion([Q0]), "cplaneType" : CPlaneType.OFFSET, "offset" : 0 * mm, "oppositeDirection" : true, "width" : 152.4 * mm, "height" : 152.4 * mm});
        }
        {
            var Q0;
            Q0=qCreatedBy(id+"F2.planeOp",FACE);
            var sketch = newSketch(context, id + "F3", { "sketchPlane" : qUnion([Q0])});
            skLineSegment(sketch, "E217", {"start": v(-203.2, -69.85) * mm, "end": v(-203.2, -88.9) * mm});
            skLineSegment(sketch, "E218", {"start": v(-203.2, -88.9) * mm, "end": v(-190.5, -88.9) * mm});
            skLineSegment(sketch, "E219", {"start": v(-190.5, -88.9) * mm, "end": v(-190.5, -114.3) * mm});
            skLineSegment(sketch, "E220", {"start": v(-190.5, -114.3) * mm, "end": v(190.5, -114.3) * mm});
            skLineSegment(sketch, "E221", {"start": v(190.5, -114.3) * mm, "end": v(190.5, -88.9) * mm});
            skLineSegment(sketch, "E222", {"start": v(190.5, -88.9) * mm, "end": v(203.2, -88.9) * mm});
            skLineSegment(sketch, "E223", {"start": v(203.2, -88.9) * mm, "end": v(203.2, -69.85) * mm});
            skLineSegment(sketch, "E224", {"start": v(203.2, -69.85) * mm, "end": v(-203.2, -69.85) * mm});
            skSolve(sketch);
        }
        {
            var Q0;
            Q0=qSketchRegion(id+"F3",true);
            extrude(context, id + "F4", {"entities" : qUnion([Q0]), "oppositeDirection" : true, "depth" : 12.7 * mm});
        }
        {
            var Q0;
            Q0=makeQuery(id+"F1.opExtrude","CAP_FACE",FACE,{"disambiguationData":[OSD([sQuery(id+"F0.wireOp",EDGE,"f3b8bc04-095d-494a-bcce-8306202adf07"),sQuery(id+"F0.wireOp",EDGE,"08e92012-2e21-4d94-9f0a-c8e57075e395"),sQuery(id+"F0.wireOp",EDGE,"122fa739-26d1-4298-ae19-82ac91bd4e23"),sQuery(id+"F0.wireOp",EDGE,"d5e32c5b-27bd-42dd-9b3f-d947ba78b5c6"),sQuery(id+"F0.wireOp",EDGE,"E0"),sQuery(id+"F0.wireOp",EDGE,"E1"),sQuery(id+"F0.wireOp",EDGE,"E2"),sQuery(id+"F0.wireOp",EDGE,"E3"),sQuery(id+"F0.wireOp",EDGE,"E4"),sQuery(id+"F0.wireOp",EDGE,"E5"),sQuery(id+"F0.wireOp",EDGE,"E6"),sQuery(id+"F0.wireOp",EDGE,"E7"),sQuery(id+"F0.wireOp",EDGE,"E8"),sQuery(id+"F0.wireOp",EDGE,"E9"),sQuery(id+"F0.wireOp",EDGE,"E10"),sQuery(id+"F0.wireOp",EDGE,"E11"),sQuery(id+"F0.wireOp",EDGE,"E12"),sQuery(id+"F0.wireOp",EDGE,"E13"),sQuery(id+"F0.wireOp",EDGE,"E14"),sQuery(id+"F0.wireOp",EDGE,"E15"),sQuery(id+"F0.wireOp",EDGE,"E16"),sQuery(id+"F0.wireOp",EDGE,"E17"),sQuery(id+"F0.wireOp",EDGE,"E18"),sQuery(id+"F0.wireOp",EDGE,"E19"),sQuery(id+"F0.wireOp",EDGE,"E20"),sQuery(id+"F0.wireOp",EDGE,"E21"),sQuery(id+"F0.wireOp",EDGE,"E22"),sQuery(id+"F0.wireOp",EDGE,"E23"),sQuery(id+"F0.wireOp",EDGE,"E24"),sQuery(id+"F0.wireOp",EDGE,"E25"),sQuery(id+"F0.wireOp",EDGE,"E26"),sQuery(id+"F0.wireOp",EDGE,"E27"),sQuery(id+"F0.wireOp",EDGE,"E28"),sQuery(id+"F0.wireOp",EDGE,"E29"),sQuery(id+"F0.wireOp",EDGE,"E30"),sQuery(id+"F0.wireOp",EDGE,"E31"),sQuery(id+"F0.wireOp",EDGE,"E32"),sQuery(id+"F0.wireOp",EDGE,"E33"),sQuery(id+"F0.wireOp",EDGE,"E34"),sQuery(id+"F0.wireOp",EDGE,"E35"),sQuery(id+"F0.wireOp",EDGE,"E36"),sQuery(id+"F0.wireOp",EDGE,"E37"),sQuery(id+"F0.wireOp",EDGE,"E38"),sQuery(id+"F0.wireOp",EDGE,"E39"),sQuery(id+"F0.wireOp",EDGE,"E40"),sQuery(id+"F0.wireOp",EDGE,"E41"),sQuery(id+"F0.wireOp",EDGE,"E42"),sQuery(id+"F0.wireOp",EDGE,"E43"),sQuery(id+"F0.wireOp",EDGE,"E44"),sQuery(id+"F0.wireOp",EDGE,"E45"),sQuery(id+"F0.wireOp",EDGE,"E46"),sQuery(id+"F0.wireOp",EDGE,"E47"),sQuery(id+"F0.wireOp",EDGE,"E48"),sQuery(id+"F0.wireOp",EDGE,"E49"),sQuery(id+"F0.wireOp",EDGE,"E50"),sQuery(id+"F0.wireOp",EDGE,"E51"),sQuery(id+"F0.wireOp",EDGE,"E52"),sQuery(id+"F0.wireOp",EDGE,"E53"),sQuery(id+"F0.wireOp",EDGE,"E54"),sQuery(id+"F0.wireOp",EDGE,"E55"),sQuery(id+"F0.wireOp",EDGE,"E56"),sQuery(id+"F0.wireOp",EDGE,"E57"),sQuery(id+"F0.wireOp",EDGE,"E58"),sQuery(id+"F0.wireOp",EDGE,"E59"),sQuery(id+"F0.wireOp",EDGE,"E60"),sQuery(id+"F0.wireOp",EDGE,"E61"),sQuery(id+"F0.wireOp",EDGE,"E62"),sQuery(id+"F0.wireOp",EDGE,"E63"),sQuery(id+"F0.wireOp",EDGE,"E64"),sQuery(id+"F0.wireOp",EDGE,"E65"),sQuery(id+"F0.wireOp",EDGE,"E66"),sQuery(id+"F0.wireOp",EDGE,"E67"),sQuery(id+"F0.wireOp",EDGE,"E68"),sQuery(id+"F0.wireOp",EDGE,"E69"),sQuery(id+"F0.wireOp",EDGE,"E70"),sQuery(id+"F0.wireOp",EDGE,"E71"),sQuery(id+"F0.wireOp",EDGE,"E72"),sQuery(id+"F0.wireOp",EDGE,"E73"),sQuery(id+"F0.wireOp",EDGE,"E74"),sQuery(id+"F0.wireOp",EDGE,"E75"),sQuery(id+"F0.wireOp",EDGE,"E76"),sQuery(id+"F0.wireOp",EDGE,"E77"),sQuery(id+"F0.wireOp",EDGE,"E78"),sQuery(id+"F0.wireOp",EDGE,"E79"),sQuery(id+"F0.wireOp",EDGE,"E80"),sQuery(id+"F0.wireOp",EDGE,"E81"),sQuery(id+"F0.wireOp",EDGE,"E82"),sQuery(id+"F0.wireOp",EDGE,"E83"),sQuery(id+"F0.wireOp",EDGE,"E84"),sQuery(id+"F0.wireOp",EDGE,"E85"),sQuery(id+"F0.wireOp",EDGE,"2d70706d-4c91-45b7-b293-bf747273fc1e"),sQuery(id+"F0.wireOp",EDGE,"f606c3c6-6e26-49ba-bb4a-ffbf22b89f78"),sQuery(id+"F0.wireOp",EDGE,"6ded5a20-7a3f-46e3-8459-1bb58dbc2f72"),sQuery(id+"F0.wireOp",EDGE,"099ca5a8-81e7-49d1-b38d-3a86f93f5891"),sQuery(id+"F0.wireOp",EDGE,"E86"),sQuery(id+"F0.wireOp",EDGE,"E87"),sQuery(id+"F0.wireOp",EDGE,"E88"),sQuery(id+"F0.wireOp",EDGE,"E89"),sQuery(id+"F0.wireOp",EDGE,"E90"),sQuery(id+"F0.wireOp",EDGE,"E91"),sQuery(id+"F0.wireOp",EDGE,"E92"),sQuery(id+"F0.wireOp",EDGE,"E93")])],"isStart":true});
            cPlane(context, id + "F5", {"entities" : qUnion([Q0]), "cplaneType" : CPlaneType.OFFSET, "offset" : 6.35 * mm, "oppositeDirection" : true, "width" : 152.4 * mm, "height" : 152.4 * mm});
        }
        {
            var Q0;
            Q0=qCreatedBy(id+"F2.planeOp",FACE);
            var sketch = newSketch(context, id + "F6", { "sketchPlane" : qUnion([Q0])});
            skLineSegment(sketch, "E225", {"start": v(-225.43, 44.45) * mm, "end": v(-225.43, -99.06) * mm});
            skArc(sketch, "E226", {"start": v(-225.42, -99.06) * mm, "mid": v(-224.68, -100.86) * mm, "end": v(-222.88, -101.6) * mm});
            skLineSegment(sketch, "E227", {"start": v(-222.88, -101.6) * mm, "end": v(222.88, -101.6) * mm});
            skArc(sketch, "E228", {"start": v(222.88, -101.6) * mm, "mid": v(224.68, -100.86) * mm, "end": v(225.42, -99.06) * mm});
            skLineSegment(sketch, "E229", {"start": v(225.43, -157.48) * mm, "end": v(225.42, 151.13) * mm});
            skArc(sketch, "E230", {"start": v(225.42, 151.13) * mm, "mid": v(224.68, 152.93) * mm, "end": v(222.88, 153.67) * mm});
            skLineSegment(sketch, "E231", {"start": v(222.88, 153.67) * mm, "end": v(206.63, 153.67) * mm});
            skArc(sketch, "E232", {"start": v(206.63, 153.67) * mm, "mid": v(204.83, 152.93) * mm, "end": v(204.09, 151.13) * mm});
            skLineSegment(sketch, "E233", {"start": v(204.09, 151.13) * mm, "end": v(204.09, 144.24) * mm});
            skArc(sketch, "E234", {"start": v(193.92, 62.35) * mm, "mid": v(201.07, 64.9) * mm, "end": v(204.09, 71.85) * mm});
            skLineSegment(sketch, "E235", {"start": v(193.92, 62.35) * mm, "end": v(140.8, 65.96) * mm});
            skArc(sketch, "E236", {"start": v(139.09, 66.32) * mm, "mid": v(139.93, 66.08) * mm, "end": v(140.8, 65.96) * mm});
            skLineSegment(sketch, "E237", {"start": v(139.09, 66.32) * mm, "end": v(120.24, 73.06) * mm});
            skArc(sketch, "E238", {"start": v(113.92, 82.03) * mm, "mid": v(115.66, 76.54) * mm, "end": v(120.24, 73.06) * mm});
            skLineSegment(sketch, "E239", {"start": v(113.92, 82.03) * mm, "end": v(113.92, 90.6) * mm});
            skArc(sketch, "E240", {"start": v(113.92, 90.6) * mm, "mid": v(113.3, 92.26) * mm, "end": v(111.74, 93.1) * mm});
            skLineSegment(sketch, "E241", {"start": v(111.74, 93.1) * mm, "end": v(100.3, 94.74) * mm});
            skArc(sketch, "E242", {"start": v(100.3, 94.74) * mm, "mid": v(98.28, 94.15) * mm, "end": v(97.4, 92.23) * mm});
            skLineSegment(sketch, "E243", {"start": v(97.4, 92.23) * mm, "end": v(97.4, 85.4) * mm});
            skArc(sketch, "E244", {"start": v(78.36, 85.4) * mm, "mid": v(87.88, 75.87) * mm, "end": v(97.4, 85.4) * mm});
            skLineSegment(sketch, "E245", {"start": v(78.36, 85.4) * mm, "end": v(78.36, 95.67) * mm});
            skArc(sketch, "E246", {"start": v(78.36, 95.67) * mm, "mid": v(77.74, 97.34) * mm, "end": v(76.18, 98.19) * mm});
            skLineSegment(sketch, "E247", {"start": v(76.18, 98.19) * mm, "end": v(64.75, 99.82) * mm});
            skArc(sketch, "E248", {"start": v(64.75, 99.82) * mm, "mid": v(62.72, 99.23) * mm, "end": v(61.85, 97.3) * mm});
            skLineSegment(sketch, "E249", {"start": v(61.85, 97.3) * mm, "end": v(61.85, 87.64) * mm});
            skArc(sketch, "E250", {"start": v(42.8, 87.64) * mm, "mid": v(52.32, 78.12) * mm, "end": v(61.85, 87.64) * mm});
            skLineSegment(sketch, "E251", {"start": v(42.8, 87.64) * mm, "end": v(42.8, 99.06) * mm});
            skArc(sketch, "E252", {"start": v(42.8, 99.06) * mm, "mid": v(42.06, 100.86) * mm, "end": v(40.26, 101.6) * mm});
            skLineSegment(sketch, "E253", {"start": v(40.26, 101.6) * mm, "end": v(28.83, 101.6) * mm});
            skArc(sketch, "E254", {"start": v(28.83, 101.6) * mm, "mid": v(27.03, 100.86) * mm, "end": v(26.29, 99.06) * mm});
            skLineSegment(sketch, "E255", {"start": v(26.29, 99.06) * mm, "end": v(26.29, 88.76) * mm});
            skArc(sketch, "E256", {"start": v(7.24, 88.76) * mm, "mid": v(16.76, 79.24) * mm, "end": v(26.29, 88.76) * mm});
            skLineSegment(sketch, "E257", {"start": v(7.24, 88.76) * mm, "end": v(7.24, 99.06) * mm});
            skArc(sketch, "E258", {"start": v(7.24, 99.06) * mm, "mid": v(6.5, 100.86) * mm, "end": v(4.7, 101.6) * mm});
            skLineSegment(sketch, "E259", {"start": v(4.7, 101.6) * mm, "end": v(-6.73, 101.6) * mm});
            skArc(sketch, "E260", {"start": v(-6.73, 101.6) * mm, "mid": v(-8.53, 100.86) * mm, "end": v(-9.27, 99.06) * mm});
            skLineSegment(sketch, "E261", {"start": v(-9.27, 99.06) * mm, "end": v(-9.27, 88.76) * mm});
            skArc(sketch, "E262", {"start": v(-28.32, 88.76) * mm, "mid": v(-18.8, 79.24) * mm, "end": v(-9.27, 88.76) * mm});
            skLineSegment(sketch, "E263", {"start": v(-28.32, 88.76) * mm, "end": v(-28.32, 99.06) * mm});
            skArc(sketch, "E264", {"start": v(-28.32, 99.06) * mm, "mid": v(-29.06, 100.86) * mm, "end": v(-30.86, 101.6) * mm});
            skLineSegment(sketch, "E265", {"start": v(-30.86, 101.6) * mm, "end": v(-42.3, 101.6) * mm});
            skArc(sketch, "E266", {"start": v(-42.3, 101.6) * mm, "mid": v(-44.09, 100.86) * mm, "end": v(-44.83, 99.06) * mm});
            skLineSegment(sketch, "E267", {"start": v(-44.83, 99.06) * mm, "end": v(-44.83, 87.64) * mm});
            skArc(sketch, "E268", {"start": v(-63.88, 87.64) * mm, "mid": v(-54.36, 78.12) * mm, "end": v(-44.83, 87.64) * mm});
            skLineSegment(sketch, "E269", {"start": v(-63.88, 87.64) * mm, "end": v(-63.88, 97.3) * mm});
            skArc(sketch, "E270", {"start": v(-63.88, 97.3) * mm, "mid": v(-64.76, 99.22) * mm, "end": v(-66.78, 99.82) * mm});
            skLineSegment(sketch, "E271", {"start": v(-66.78, 99.82) * mm, "end": v(-78.21, 98.19) * mm});
            skArc(sketch, "E272", {"start": v(-78.21, 98.19) * mm, "mid": v(-79.77, 97.34) * mm, "end": v(-80.4, 95.67) * mm});
            skLineSegment(sketch, "E273", {"start": v(-80.4, 95.67) * mm, "end": v(-80.4, 85.4) * mm});
            skArc(sketch, "E274", {"start": v(-99.44, 85.4) * mm, "mid": v(-89.92, 75.87) * mm, "end": v(-80.4, 85.4) * mm});
            skLineSegment(sketch, "E275", {"start": v(-99.44, 85.4) * mm, "end": v(-99.44, 92.22) * mm});
            skArc(sketch, "E276", {"start": v(-99.44, 92.22) * mm, "mid": v(-100.32, 94.14) * mm, "end": v(-102.34, 94.74) * mm});
            skLineSegment(sketch, "E277", {"start": v(-102.34, 94.74) * mm, "end": v(-113.77, 93.1) * mm});
            skArc(sketch, "E278", {"start": v(-113.77, 93.1) * mm, "mid": v(-115.33, 92.26) * mm, "end": v(-115.95, 90.6) * mm});
            skLineSegment(sketch, "E279", {"start": v(-115.95, 90.6) * mm, "end": v(-115.95, 82.03) * mm});
            skArc(sketch, "E280", {"start": v(-122.27, 73.06) * mm, "mid": v(-117.69, 76.54) * mm, "end": v(-115.95, 82.03) * mm});
            skLineSegment(sketch, "E281", {"start": v(-122.27, 73.06) * mm, "end": v(-141.12, 66.32) * mm});
            skArc(sketch, "E282", {"start": v(-143.97, 65.99) * mm, "mid": v(-142.53, 65.99) * mm, "end": v(-141.12, 66.32) * mm});
            skLineSegment(sketch, "E283", {"start": v(-143.97, 65.99) * mm, "end": v(-162.11, 68.05) * mm});
            skArc(sketch, "E284", {"start": v(-170.56, 77.52) * mm, "mid": v(-168.14, 71.17) * mm, "end": v(-162.11, 68.05) * mm});
            skLineSegment(sketch, "E285", {"start": v(-170.56, 77.52) * mm, "end": v(-170.56, 82.06) * mm});
            skArc(sketch, "E286", {"start": v(-170.56, 82.06) * mm, "mid": v(-171.44, 83.98) * mm, "end": v(-173.46, 84.58) * mm});
            skLineSegment(sketch, "E287", {"start": v(-173.46, 84.58) * mm, "end": v(-184.9, 82.94) * mm});
            skArc(sketch, "E288", {"start": v(-184.9, 82.94) * mm, "mid": v(-186.45, 82.1) * mm, "end": v(-187.07, 80.43) * mm});
            skLineSegment(sketch, "E289", {"start": v(-187.07, 80.43) * mm, "end": v(-187.07, 57.15) * mm});
            skArc(sketch, "E290", {"start": v(-189.61, 54.61) * mm, "mid": v(-187.81, 55.35) * mm, "end": v(-187.07, 57.15) * mm});
            skLineSegment(sketch, "E291", {"start": v(-189.61, 54.61) * mm, "end": v(-209.27, 54.61) * mm});
            skArc(sketch, "E292", {"start": v(-209.27, 54.6) * mm, "mid": v(-211.06, 53.87) * mm, "end": v(-211.8, 52.07) * mm});
            skLineSegment(sketch, "E293", {"start": v(-211.8, 52.07) * mm, "end": v(-211.8, 49.53) * mm});
            skArc(sketch, "E294", {"start": v(-214.35, 47) * mm, "mid": v(-212.55, 47.73) * mm, "end": v(-211.8, 49.53) * mm});
            skLineSegment(sketch, "E295", {"start": v(-214.35, 47) * mm, "end": v(-222.89, 47) * mm});
            skArc(sketch, "E296", {"start": v(-222.89, 47) * mm, "mid": v(-224.68, 46.25) * mm, "end": v(-225.43, 44.45) * mm});
            skLineSegment(sketch, "E297", {"start": v(-47.6, 28.79) * mm, "end": v(47.6, 28.79) * mm});
            skArc(sketch, "E298", {"start": v(-53.95, 35.14) * mm, "mid": v(-52.09, 30.65) * mm, "end": v(-47.6, 28.79) * mm});
            skLineSegment(sketch, "E299", {"start": v(-53.95, 54.19) * mm, "end": v(-53.95, 35.14) * mm});
            skArc(sketch, "E300", {"start": v(-47.6, 60.54) * mm, "mid": v(-52.09, 58.68) * mm, "end": v(-53.95, 54.19) * mm});
            skLineSegment(sketch, "E301", {"start": v(47.6, 60.54) * mm, "end": v(-47.6, 60.54) * mm});
            skArc(sketch, "E302", {"start": v(53.95, 54.19) * mm, "mid": v(52.09, 58.68) * mm, "end": v(47.6, 60.54) * mm});
            skLineSegment(sketch, "E303", {"start": v(53.95, 35.14) * mm, "end": v(53.95, 54.19) * mm});
            skArc(sketch, "E304", {"start": v(47.6, 28.79) * mm, "mid": v(52.09, 30.65) * mm, "end": v(53.95, 35.14) * mm});
            skLineSegment(sketch, "E305.0", {"start": v(225.43, 0) * mm, "end": v(-225.43, 0) * mm});
            skArc(sketch, "E306", {"start": v(-222.25, 0) * mm, "mid": v(-224.5, -0.93) * mm, "end": v(-225.43, -3.18) * mm});
            skArc(sketch, "E307", {"start": v(225.42, -3.17) * mm, "mid": v(224.5, -0.93) * mm, "end": v(222.25, 0) * mm});
            skSolve(sketch);
        }
        {
            var Q0;
            {var subQ1=sQuery(id+"F6.wireOp",EDGE,"E226");Q0=makeQuery(id+"F6.imprint","IMPRINT",FACE,{"disambiguationData":[TD([[makeQuery(id+"F6.imprint","IMPRINT",EDGE,{"derivedFrom":subQ1}),1.0]])]});}
            extrude(context, id + "F7", {"entities" : qUnion([Q0]), "depth" : 5.08 * mm, "offsetDistance" : 25.4 * mm});
        }
        {
            var Q0;
            Q0=makeQuery(id+"F7.opExtrude","CAP_FACE",FACE,{"disambiguationData":[OSD([sQuery(id+"F6.wireOp",EDGE,"765eaaff-3c03-4aed-97cd-0da59d786b2a"),sQuery(id+"F6.wireOp",EDGE,"bfbbba31-eefb-4337-b840-f57609f327d5"),sQuery(id+"F6.wireOp",EDGE,"d9fe1464-95a0-43a8-9d73-98f239073346"),sQuery(id+"F6.wireOp",EDGE,"3dbae0e5-671e-48e1-8151-e821474c8e52"),sQuery(id+"F6.wireOp",EDGE,"E225"),sQuery(id+"F6.wireOp",EDGE,"E226"),sQuery(id+"F6.wireOp",EDGE,"E227"),sQuery(id+"F6.wireOp",EDGE,"E228"),sQuery(id+"F6.wireOp",EDGE,"E229"),sQuery(id+"F6.wireOp",EDGE,"E230"),sQuery(id+"F6.wireOp",EDGE,"E231"),sQuery(id+"F6.wireOp",EDGE,"E232"),sQuery(id+"F6.wireOp",EDGE,"E233"),sQuery(id+"F6.wireOp",EDGE,"E234"),sQuery(id+"F6.wireOp",EDGE,"E235"),sQuery(id+"F6.wireOp",EDGE,"E236"),sQuery(id+"F6.wireOp",EDGE,"E237"),sQuery(id+"F6.wireOp",EDGE,"E238"),sQuery(id+"F6.wireOp",EDGE,"E239"),sQuery(id+"F6.wireOp",EDGE,"E240"),sQuery(id+"F6.wireOp",EDGE,"E241"),sQuery(id+"F6.wireOp",EDGE,"E242"),sQuery(id+"F6.wireOp",EDGE,"E243"),sQuery(id+"F6.wireOp",EDGE,"E244"),sQuery(id+"F6.wireOp",EDGE,"E245"),sQuery(id+"F6.wireOp",EDGE,"E246"),sQuery(id+"F6.wireOp",EDGE,"E247"),sQuery(id+"F6.wireOp",EDGE,"E248"),sQuery(id+"F6.wireOp",EDGE,"E249"),sQuery(id+"F6.wireOp",EDGE,"E250"),sQuery(id+"F6.wireOp",EDGE,"E251"),sQuery(id+"F6.wireOp",EDGE,"E252"),sQuery(id+"F6.wireOp",EDGE,"E253"),sQuery(id+"F6.wireOp",EDGE,"E254"),sQuery(id+"F6.wireOp",EDGE,"E255"),sQuery(id+"F6.wireOp",EDGE,"E256"),sQuery(id+"F6.wireOp",EDGE,"E257"),sQuery(id+"F6.wireOp",EDGE,"E258"),sQuery(id+"F6.wireOp",EDGE,"E259"),sQuery(id+"F6.wireOp",EDGE,"E260"),sQuery(id+"F6.wireOp",EDGE,"E261"),sQuery(id+"F6.wireOp",EDGE,"E262"),sQuery(id+"F6.wireOp",EDGE,"E263"),sQuery(id+"F6.wireOp",EDGE,"E264"),sQuery(id+"F6.wireOp",EDGE,"E265"),sQuery(id+"F6.wireOp",EDGE,"E266"),sQuery(id+"F6.wireOp",EDGE,"E267"),sQuery(id+"F6.wireOp",EDGE,"E268"),sQuery(id+"F6.wireOp",EDGE,"E269"),sQuery(id+"F6.wireOp",EDGE,"E270"),sQuery(id+"F6.wireOp",EDGE,"E271"),sQuery(id+"F6.wireOp",EDGE,"E272"),sQuery(id+"F6.wireOp",EDGE,"E273"),sQuery(id+"F6.wireOp",EDGE,"E274"),sQuery(id+"F6.wireOp",EDGE,"E275"),sQuery(id+"F6.wireOp",EDGE,"E276"),sQuery(id+"F6.wireOp",EDGE,"E277"),sQuery(id+"F6.wireOp",EDGE,"E278"),sQuery(id+"F6.wireOp",EDGE,"E279"),sQuery(id+"F6.wireOp",EDGE,"E280"),sQuery(id+"F6.wireOp",EDGE,"E281"),sQuery(id+"F6.wireOp",EDGE,"E282"),sQuery(id+"F6.wireOp",EDGE,"E283"),sQuery(id+"F6.wireOp",EDGE,"E284"),sQuery(id+"F6.wireOp",EDGE,"E285"),sQuery(id+"F6.wireOp",EDGE,"E286"),sQuery(id+"F6.wireOp",EDGE,"E287"),sQuery(id+"F6.wireOp",EDGE,"E288"),sQuery(id+"F6.wireOp",EDGE,"E289"),sQuery(id+"F6.wireOp",EDGE,"E290"),sQuery(id+"F6.wireOp",EDGE,"E291"),sQuery(id+"F6.wireOp",EDGE,"E292"),sQuery(id+"F6.wireOp",EDGE,"E293"),sQuery(id+"F6.wireOp",EDGE,"E294"),sQuery(id+"F6.wireOp",EDGE,"E295"),sQuery(id+"F6.wireOp",EDGE,"E296"),sQuery(id+"F6.wireOp",EDGE,"E297"),sQuery(id+"F6.wireOp",EDGE,"E298"),sQuery(id+"F6.wireOp",EDGE,"E299"),sQuery(id+"F6.wireOp",EDGE,"E300"),sQuery(id+"F6.wireOp",EDGE,"E301"),sQuery(id+"F6.wireOp",EDGE,"E302"),sQuery(id+"F6.wireOp",EDGE,"E303"),sQuery(id+"F6.wireOp",EDGE,"E304"),sQuery(id+"F6.wireOp",EDGE,"f9493e98-5abe-4126-86ac-bdb0b4f7d6da"),sQuery(id+"F6.wireOp",EDGE,"112f2961-29c0-47fd-bd17-f927e6cd5f86"),sQuery(id+"F6.wireOp",EDGE,"d182d45b-51f4-4f19-bbab-538119165d43"),sQuery(id+"F6.wireOp",EDGE,"f2dcc7ce-426b-4624-9908-b4b424994630")])],"isStart":false});
            var sketch = newSketch(context, id + "F8", { "sketchPlane" : qUnion([Q0])});
            skLineSegment(sketch, "E308", {"start": v(225.43, -92.22) * mm, "end": v(47.24, -92.22) * mm, "construction": true});
            skLineSegment(sketch, "E309", {"start": v(47.24, -92.22) * mm, "end": v(11.43, -92.22) * mm, "construction": true});
            skCircle(sketch, "E310", {"center": v(11.43, -92.22) * mm, "radius": 6.35 * mm, "construction": true});
            skLineSegment(sketch, "E311.bottom", {"start": v(-39.37, -76.2) * mm, "end": v(39.37, -76.2) * mm});
            skLineSegment(sketch, "E311.top", {"start": v(-39.37, -101.6) * mm, "end": v(39.37, -101.6) * mm});
            skLineSegment(sketch, "E311.left", {"start": v(-39.37, -76.2) * mm, "end": v(-39.37, -101.6) * mm});
            skLineSegment(sketch, "E311.right", {"start": v(39.37, -76.2) * mm, "end": v(39.37, -101.6) * mm});
            skLineSegment(sketch, "E312", {"start": v(11.43, -92.22) * mm, "end": v(-13.97, -92.22) * mm, "construction": true});
            skCircle(sketch, "E313", {"center": v(-13.97, -92.22) * mm, "radius": 6.35 * mm, "construction": true});
            skArc(sketch, "E314", {"start": v(-42.55, -101.6) * mm, "mid": v(-40.3, -100.67) * mm, "end": v(-39.37, -98.42) * mm});
            skArc(sketch, "E315", {"start": v(-36.2, -76.2) * mm, "mid": v(-38.44, -77.13) * mm, "end": v(-39.37, -79.37) * mm});
            skArc(sketch, "E316", {"start": v(39.37, -98.42) * mm, "mid": v(40.3, -100.67) * mm, "end": v(42.55, -101.6) * mm});
            skArc(sketch, "E317", {"start": v(39.37, -79.37) * mm, "mid": v(38.44, -77.13) * mm, "end": v(36.2, -76.2) * mm});
            skSolve(sketch);
        }
        {
            var Q0;
            {var subQ3=sQuery(id+"F8.wireOp",EDGE,"E311.top");Q0=makeQuery(id+"F8.imprint","IMPRINT",FACE,{"disambiguationData":[TD([[makeQuery(id+"F8.imprint","IMPRINT",EDGE,{"derivedFrom":subQ3}),1.0]])]});}
            var Q1;
            {var subQ3=sQuery(id+"F8.wireOp",EDGE,"E314");Q1=makeQuery(id+"F8.imprint","IMPRINT",FACE,{"disambiguationData":[TD([[makeQuery(id+"F8.imprint","IMPRINT",EDGE,{"derivedFrom":subQ3}),-1.0]])]});}
            var Q2;
            {var subQ3=sQuery(id+"F8.wireOp",EDGE,"E316");Q2=makeQuery(id+"F8.imprint","IMPRINT",FACE,{"disambiguationData":[TD([[makeQuery(id+"F8.imprint","IMPRINT",EDGE,{"derivedFrom":subQ3}),-1.0]])]});}
            extrude(context, id + "F9", {"entities" : qUnion([Q0, Q1, Q2]), "operationType" : NewBodyOperationType.REMOVE, "oppositeDirection" : true, "depth" : 6.35 * mm});
        }
        {
            var Q0;
            Q0=makeQuery(id+"F7.opExtrude","CAP_FACE",FACE,{"disambiguationData":[OSD([sQuery(id+"F6.wireOp",EDGE,"E225"),sQuery(id+"F6.wireOp",EDGE,"E226"),sQuery(id+"F6.wireOp",EDGE,"E227"),sQuery(id+"F6.wireOp",EDGE,"E228"),sQuery(id+"F6.wireOp",EDGE,"E229"),sQuery(id+"F6.wireOp",EDGE,"E305.0")])],"isStart":true});
            var sketch = newSketch(context, id + "F10", { "sketchPlane" : qUnion([Q0])});
            skLineSegment(sketch, "E318.top", {"start": v(-53.34, -46.99) * mm, "end": v(-25.4, -46.99) * mm});
            skLineSegment(sketch, "E318.right", {"start": v(-25.4, -31.75) * mm, "end": v(-25.4, -46.99) * mm});
            skLineSegment(sketch, "E319.bottom", {"start": v(-53.34, -46.99) * mm, "end": v(-53.34, -46.99) * mm});
            skLineSegment(sketch, "E320", {"start": v(-53.34, -46.99) * mm, "end": v(-53.34, -31.75) * mm});
            skLineSegment(sketch, "E321", {"start": v(-53.34, -31.75) * mm, "end": v(-25.4, -31.75) * mm});
            skLineSegment(sketch, "E322", {"start": v(-53.34, -41.9) * mm, "end": v(-95.25, 0) * mm});
            skLineSegment(sketch, "E323", {"start": v(-41.95, -31.75) * mm, "end": v(-73.7, 0) * mm});
            skLineSegment(sketch, "E324.0", {"start": v(-222.25, 0) * mm, "end": v(222.25, 0) * mm});
            skLineSegment(sketch, "E325", {"start": v(0, 0) * mm, "end": v(0, -98.96) * mm, "construction": true});
            skArc(sketch, "E326", {"start": v(-49.39, -24.31) * mm, "mid": v(-41.15, -29.82) * mm, "end": v(-31.43, -31.75) * mm});
            skArc(sketch, "E327", {"start": v(-85.95, -9.3) * mm, "mid": v(-96.25, -2.42) * mm, "end": v(-108.4, 0) * mm});
            skArc(sketch, "E328", {"start": v(-58.37, 0) * mm, "mid": v(-64.23, -3.92) * mm, "end": v(-62.86, -10.84) * mm});
            skArc(sketch, "E329", {"start": v(-53.34, -43.23) * mm, "mid": v(-53.58, -42.01) * mm, "end": v(-54.27, -40.98) * mm});
            skArc(sketch, "E330", {"start": v(-53.34, -43.81) * mm, "mid": v(-52.41, -46.06) * mm, "end": v(-50.17, -46.99) * mm});
            skArc(sketch, "E331", {"start": v(-25.4, -34.92) * mm, "mid": v(-26.33, -32.68) * mm, "end": v(-28.58, -31.75) * mm});
            skArc(sketch, "E332", {"start": v(-28.58, -46.99) * mm, "mid": v(-26.33, -46.06) * mm, "end": v(-25.4, -43.81) * mm});
            skArc(sketch, "E333.MirrorCS", {"start": v(58.37, 0) * mm, "mid": v(64.23, -3.92) * mm, "end": v(62.86, -10.84) * mm});
            skLineSegment(sketch, "E334.MirrorCS", {"start": v(41.95, -31.75) * mm, "end": v(73.7, 0) * mm});
            skArc(sketch, "E335.MirrorCS", {"start": v(49.39, -24.31) * mm, "mid": v(41.15, -29.82) * mm, "end": v(31.43, -31.75) * mm});
            skLineSegment(sketch, "E336.MirrorCS", {"start": v(53.34, -31.75) * mm, "end": v(25.4, -31.75) * mm});
            skArc(sketch, "E337.MirrorCS", {"start": v(25.4, -34.92) * mm, "mid": v(26.33, -32.68) * mm, "end": v(28.57, -31.75) * mm});
            skLineSegment(sketch, "E338.MirrorCS", {"start": v(25.4, -31.75) * mm, "end": v(25.4, -46.99) * mm});
            skArc(sketch, "E339.MirrorCS", {"start": v(28.58, -46.99) * mm, "mid": v(26.33, -46.06) * mm, "end": v(25.4, -43.81) * mm});
            skLineSegment(sketch, "E340.MirrorCS", {"start": v(53.34, -46.99) * mm, "end": v(25.4, -46.99) * mm});
            skArc(sketch, "E341.MirrorCS", {"start": v(53.34, -43.81) * mm, "mid": v(52.41, -46.06) * mm, "end": v(50.17, -46.99) * mm});
            skLineSegment(sketch, "E342.MirrorCS", {"start": v(53.34, -46.99) * mm, "end": v(53.34, -31.75) * mm});
            skArc(sketch, "E343.MirrorCS", {"start": v(53.34, -43.23) * mm, "mid": v(53.58, -42.01) * mm, "end": v(54.27, -40.98) * mm});
            skLineSegment(sketch, "E344.MirrorCS", {"start": v(53.34, -41.9) * mm, "end": v(95.25, 0) * mm});
            skArc(sketch, "E345.MirrorCS", {"start": v(85.95, -9.3) * mm, "mid": v(96.25, -2.42) * mm, "end": v(108.4, 0) * mm});
            skSolve(sketch);
        }
        {
            var Q0;
            {var subQ3=sQuery(id+"F10.wireOp",EDGE,"E321");var subQ4=sQuery(id+"F10.wireOp",EDGE,"E320");var subQ5=makeQuery(id+"F10.imprint","INTERSECT",VERTEX,{"derivedFrom":[subQ4,subQ3]});Q0=makeQuery(id+"F10.imprint","IMPRINT",FACE,{"disambiguationData":[TD([[makeQuery(id+"F10.imprint","IMPRINT",EDGE,{"disambiguationData":[TD([[subQ5,1.0]])],"derivedFrom":subQ4}),1.0]])]});}
            var Q1;
            {var subQ3=sQuery(id+"F10.wireOp",EDGE,"E326");Q1=makeQuery(id+"F10.imprint","IMPRINT",FACE,{"disambiguationData":[TD([[makeQuery(id+"F10.imprint","IMPRINT",EDGE,{"derivedFrom":subQ3}),-1.0]])]});}
            var Q2;
            {var subQ3=sQuery(id+"F10.wireOp",EDGE,"E328");Q2=makeQuery(id+"F10.imprint","IMPRINT",FACE,{"disambiguationData":[TD([[makeQuery(id+"F10.imprint","IMPRINT",EDGE,{"derivedFrom":subQ3}),-1.0]])]});}
            var Q3;
            {var subQ3=sQuery(id+"F10.wireOp",EDGE,"E327");Q3=makeQuery(id+"F10.imprint","IMPRINT",FACE,{"disambiguationData":[TD([[makeQuery(id+"F10.imprint","IMPRINT",EDGE,{"derivedFrom":subQ3}),-1.0]])]});}
            var Q4;
            {var subQ7=sQuery(id+"F10.wireOp",EDGE,"E330");Q4=makeQuery(id+"F10.imprint","IMPRINT",FACE,{"disambiguationData":[TD([[makeQuery(id+"F10.imprint","IMPRINT",EDGE,{"derivedFrom":subQ7}),1.0]])]});}
            var Q5;
            {var subQ3=sQuery(id+"F10.wireOp",EDGE,"E329");Q5=makeQuery(id+"F10.imprint","IMPRINT",FACE,{"disambiguationData":[TD([[makeQuery(id+"F10.imprint","IMPRINT",EDGE,{"derivedFrom":subQ3}),-1.0]])]});}
            var Q6;
            {var subQ6=sQuery(id+"F10.wireOp",EDGE,"E337.MirrorCS");Q6=makeQuery(id+"F10.imprint","IMPRINT",FACE,{"disambiguationData":[TD([[makeQuery(id+"F10.imprint","IMPRINT",EDGE,{"derivedFrom":subQ6}),-1.0]])]});}
            var Q7;
            {var subQ0=sQuery(id+"F10.wireOp",EDGE,"E334.MirrorCS");var subQ2=sQuery(id+"F10.wireOp",EDGE,"E324.0");var subQ3=makeQuery(id+"F10.imprint","INTERSECT",VERTEX,{"derivedFrom":[subQ2,subQ0]});Q7=makeQuery(id+"F10.imprint","IMPRINT",FACE,{"disambiguationData":[TD([[makeQuery(id+"F10.imprint","IMPRINT",EDGE,{"disambiguationData":[TD([[subQ3,-1.0]])],"derivedFrom":subQ2}),-1.0]])]});}
            var Q8;
            {var subQ3=sQuery(id+"F10.wireOp",EDGE,"E335.MirrorCS");Q8=makeQuery(id+"F10.imprint","IMPRINT",FACE,{"disambiguationData":[TD([[makeQuery(id+"F10.imprint","IMPRINT",EDGE,{"derivedFrom":subQ3}),1.0]])]});}
            var Q9;
            {var subQ0=sQuery(id+"F10.wireOp",EDGE,"E343.MirrorCS");Q9=makeQuery(id+"F10.imprint","IMPRINT",FACE,{"disambiguationData":[TD([[makeQuery(id+"F10.imprint","IMPRINT",EDGE,{"derivedFrom":subQ0}),1.0]])]});}
            var Q10;
            {var subQ3=sQuery(id+"F10.wireOp",EDGE,"E345.MirrorCS");Q10=makeQuery(id+"F10.imprint","IMPRINT",FACE,{"disambiguationData":[TD([[makeQuery(id+"F10.imprint","IMPRINT",EDGE,{"derivedFrom":subQ3}),1.0]])]});}
            var Q11;
            {var subQ0=sQuery(id+"F10.wireOp",EDGE,"E333.MirrorCS");Q11=makeQuery(id+"F10.imprint","IMPRINT",FACE,{"disambiguationData":[TD([[makeQuery(id+"F10.imprint","IMPRINT",EDGE,{"derivedFrom":subQ0}),1.0]])]});}
            extrude(context, id + "F11", {"entities" : qUnion([Q0, Q1, Q2, Q3, Q4, Q5, Q6, Q7, Q8, Q9, Q10, Q11]), "operationType" : NewBodyOperationType.REMOVE, "endBound" : BoundingType.THROUGH_ALL, "oppositeDirection" : true, "depth" : 25.4 * mm});
        }
        {
            var Q0;
            Q0=makeQuery(id+"F7.opExtrude","SWEPT_BODY",BODY,{"disambiguationData":[OSD([sQuery(id+"F6.wireOp",EDGE,"765eaaff-3c03-4aed-97cd-0da59d786b2a"),sQuery(id+"F6.wireOp",EDGE,"bfbbba31-eefb-4337-b840-f57609f327d5"),sQuery(id+"F6.wireOp",EDGE,"d9fe1464-95a0-43a8-9d73-98f239073346"),sQuery(id+"F6.wireOp",EDGE,"3dbae0e5-671e-48e1-8151-e821474c8e52"),sQuery(id+"F6.wireOp",EDGE,"E225"),sQuery(id+"F6.wireOp",EDGE,"E226"),sQuery(id+"F6.wireOp",EDGE,"E227"),sQuery(id+"F6.wireOp",EDGE,"E228"),sQuery(id+"F6.wireOp",EDGE,"E229"),sQuery(id+"F6.wireOp",EDGE,"E230"),sQuery(id+"F6.wireOp",EDGE,"E231"),sQuery(id+"F6.wireOp",EDGE,"E232"),sQuery(id+"F6.wireOp",EDGE,"E233"),sQuery(id+"F6.wireOp",EDGE,"E234"),sQuery(id+"F6.wireOp",EDGE,"E235"),sQuery(id+"F6.wireOp",EDGE,"E236"),sQuery(id+"F6.wireOp",EDGE,"E237"),sQuery(id+"F6.wireOp",EDGE,"E238"),sQuery(id+"F6.wireOp",EDGE,"E239"),sQuery(id+"F6.wireOp",EDGE,"E240"),sQuery(id+"F6.wireOp",EDGE,"E241"),sQuery(id+"F6.wireOp",EDGE,"E242"),sQuery(id+"F6.wireOp",EDGE,"E243"),sQuery(id+"F6.wireOp",EDGE,"E244"),sQuery(id+"F6.wireOp",EDGE,"E245"),sQuery(id+"F6.wireOp",EDGE,"E246"),sQuery(id+"F6.wireOp",EDGE,"E247"),sQuery(id+"F6.wireOp",EDGE,"E248"),sQuery(id+"F6.wireOp",EDGE,"E249"),sQuery(id+"F6.wireOp",EDGE,"E250"),sQuery(id+"F6.wireOp",EDGE,"E251"),sQuery(id+"F6.wireOp",EDGE,"E252"),sQuery(id+"F6.wireOp",EDGE,"E253"),sQuery(id+"F6.wireOp",EDGE,"E254"),sQuery(id+"F6.wireOp",EDGE,"E255"),sQuery(id+"F6.wireOp",EDGE,"E256"),sQuery(id+"F6.wireOp",EDGE,"E257"),sQuery(id+"F6.wireOp",EDGE,"E258"),sQuery(id+"F6.wireOp",EDGE,"E259"),sQuery(id+"F6.wireOp",EDGE,"E260"),sQuery(id+"F6.wireOp",EDGE,"E261"),sQuery(id+"F6.wireOp",EDGE,"E262"),sQuery(id+"F6.wireOp",EDGE,"E263"),sQuery(id+"F6.wireOp",EDGE,"E264"),sQuery(id+"F6.wireOp",EDGE,"E265"),sQuery(id+"F6.wireOp",EDGE,"E266"),sQuery(id+"F6.wireOp",EDGE,"E267"),sQuery(id+"F6.wireOp",EDGE,"E268"),sQuery(id+"F6.wireOp",EDGE,"E269"),sQuery(id+"F6.wireOp",EDGE,"E270"),sQuery(id+"F6.wireOp",EDGE,"E271"),sQuery(id+"F6.wireOp",EDGE,"E272"),sQuery(id+"F6.wireOp",EDGE,"E273"),sQuery(id+"F6.wireOp",EDGE,"E274"),sQuery(id+"F6.wireOp",EDGE,"E275"),sQuery(id+"F6.wireOp",EDGE,"E276"),sQuery(id+"F6.wireOp",EDGE,"E277"),sQuery(id+"F6.wireOp",EDGE,"E278"),sQuery(id+"F6.wireOp",EDGE,"E279"),sQuery(id+"F6.wireOp",EDGE,"E280"),sQuery(id+"F6.wireOp",EDGE,"E281"),sQuery(id+"F6.wireOp",EDGE,"E282"),sQuery(id+"F6.wireOp",EDGE,"E283"),sQuery(id+"F6.wireOp",EDGE,"E284"),sQuery(id+"F6.wireOp",EDGE,"E285"),sQuery(id+"F6.wireOp",EDGE,"E286"),sQuery(id+"F6.wireOp",EDGE,"E287"),sQuery(id+"F6.wireOp",EDGE,"E288"),sQuery(id+"F6.wireOp",EDGE,"E289"),sQuery(id+"F6.wireOp",EDGE,"E290"),sQuery(id+"F6.wireOp",EDGE,"E291"),sQuery(id+"F6.wireOp",EDGE,"E292"),sQuery(id+"F6.wireOp",EDGE,"E293"),sQuery(id+"F6.wireOp",EDGE,"E294"),sQuery(id+"F6.wireOp",EDGE,"E295"),sQuery(id+"F6.wireOp",EDGE,"E296"),sQuery(id+"F6.wireOp",EDGE,"E297"),sQuery(id+"F6.wireOp",EDGE,"E298"),sQuery(id+"F6.wireOp",EDGE,"E299"),sQuery(id+"F6.wireOp",EDGE,"E300"),sQuery(id+"F6.wireOp",EDGE,"E301"),sQuery(id+"F6.wireOp",EDGE,"E302"),sQuery(id+"F6.wireOp",EDGE,"E303"),sQuery(id+"F6.wireOp",EDGE,"E304"),sQuery(id+"F6.wireOp",EDGE,"f9493e98-5abe-4126-86ac-bdb0b4f7d6da"),sQuery(id+"F6.wireOp",EDGE,"112f2961-29c0-47fd-bd17-f927e6cd5f86"),sQuery(id+"F6.wireOp",EDGE,"d182d45b-51f4-4f19-bbab-538119165d43"),sQuery(id+"F6.wireOp",EDGE,"f2dcc7ce-426b-4624-9908-b4b424994630")])]});
            var Q1;
            Q1=qCreatedBy(id+"F5.planeOp",FACE);
            mirror(context, id + "F12", {"entities" : qUnion([Q0]), "mirrorPlane" : qUnion([Q1])});
        }
        {
            var Q0;
            Q0=makeQuery(id+"F4.opExtrude","CAP_FACE",FACE,{"disambiguationData":[OSD([sQuery(id+"F3.wireOp",EDGE,"E217"),sQuery(id+"F3.wireOp",EDGE,"E218"),sQuery(id+"F3.wireOp",EDGE,"E219"),sQuery(id+"F3.wireOp",EDGE,"E220"),sQuery(id+"F3.wireOp",EDGE,"E221"),sQuery(id+"F3.wireOp",EDGE,"E222"),sQuery(id+"F3.wireOp",EDGE,"E223"),sQuery(id+"F3.wireOp",EDGE,"E224")])],"isStart":false});
            var sketch = newSketch(context, id + "F13", { "sketchPlane" : qUnion([Q0])});
            skLineSegment(sketch, "E346.bottom", {"start": v(-225.43, -101.6) * mm, "end": v(-39.37, -101.6) * mm});
            skLineSegment(sketch, "E346.top", {"start": v(-225.43, -127) * mm, "end": v(225.43, -127) * mm});
            skLineSegment(sketch, "E346.left", {"start": v(-225.43, -101.6) * mm, "end": v(-225.43, -127) * mm});
            skLineSegment(sketch, "E346.right", {"start": v(225.43, -101.6) * mm, "end": v(225.43, -127) * mm});
            skLineSegment(sketch, "E347.bottom", {"start": v(-39.37, -76.2) * mm, "end": v(39.37, -76.2) * mm});
            skLineSegment(sketch, "E347.left", {"start": v(-39.37, -76.2) * mm, "end": v(-39.37, -101.6) * mm});
            skLineSegment(sketch, "E347.right", {"start": v(39.37, -76.2) * mm, "end": v(39.37, -101.6) * mm});
            skLineSegment(sketch, "E348.trimOffspring", {"start": v(39.37, -101.6) * mm, "end": v(225.43, -101.6) * mm});
            skArc(sketch, "E349.0.0", {"start": v(108.4, 0) * mm, "mid": v(96.25, -2.42) * mm, "end": v(85.95, -9.3) * mm});
            skLineSegment(sketch, "E349.0.1", {"start": v(108.4, 0) * mm, "end": v(222.25, 0) * mm});
            skArc(sketch, "E349.0.2", {"start": v(222.25, 0) * mm, "mid": v(224.5, -0.93) * mm, "end": v(225.43, -3.18) * mm});
            skLineSegment(sketch, "E349.0.3", {"start": v(225.43, -3.18) * mm, "end": v(225.43, -99.06) * mm});
            skArc(sketch, "E349.0.4", {"start": v(225.42, -99.06) * mm, "mid": v(224.68, -100.86) * mm, "end": v(222.88, -101.6) * mm});
            skLineSegment(sketch, "E349.0.5", {"start": v(222.88, -101.6) * mm, "end": v(42.55, -101.6) * mm});
            skArc(sketch, "E349.0.6", {"start": v(42.55, -101.6) * mm, "mid": v(40.3, -100.67) * mm, "end": v(39.37, -98.42) * mm});
            skLineSegment(sketch, "E349.0.7", {"start": v(39.37, -98.42) * mm, "end": v(39.37, -79.37) * mm});
            skArc(sketch, "E349.0.8", {"start": v(39.37, -79.37) * mm, "mid": v(38.44, -77.13) * mm, "end": v(36.2, -76.2) * mm});
            skLineSegment(sketch, "E349.0.9", {"start": v(36.2, -76.2) * mm, "end": v(-36.2, -76.2) * mm});
            skArc(sketch, "E349.0.10", {"start": v(-36.2, -76.2) * mm, "mid": v(-38.44, -77.13) * mm, "end": v(-39.37, -79.37) * mm});
            skLineSegment(sketch, "E349.0.11", {"start": v(-39.37, -79.37) * mm, "end": v(-39.37, -98.42) * mm});
            skArc(sketch, "E349.0.12", {"start": v(-39.37, -98.42) * mm, "mid": v(-40.3, -100.67) * mm, "end": v(-42.55, -101.6) * mm});
            skLineSegment(sketch, "E349.0.13", {"start": v(-42.55, -101.6) * mm, "end": v(-222.88, -101.6) * mm});
            skArc(sketch, "E349.0.14", {"start": v(-222.88, -101.6) * mm, "mid": v(-224.68, -100.86) * mm, "end": v(-225.42, -99.06) * mm});
            skLineSegment(sketch, "E349.0.15", {"start": v(-225.43, -99.06) * mm, "end": v(-225.43, -3.17) * mm});
            skArc(sketch, "E349.0.16", {"start": v(-225.42, -3.17) * mm, "mid": v(-224.5, -0.93) * mm, "end": v(-222.25, 0) * mm});
            skLineSegment(sketch, "E349.0.17", {"start": v(-222.25, 0) * mm, "end": v(-108.4, 0) * mm});
            skArc(sketch, "E349.0.18", {"start": v(-108.4, 0) * mm, "mid": v(-96.25, -2.42) * mm, "end": v(-85.95, -9.3) * mm});
            skLineSegment(sketch, "E349.0.19", {"start": v(-85.95, -9.3) * mm, "end": v(-54.27, -40.98) * mm});
            skArc(sketch, "E349.0.20", {"start": v(-54.27, -40.98) * mm, "mid": v(-53.58, -42.01) * mm, "end": v(-53.34, -43.23) * mm});
            skLineSegment(sketch, "E349.0.21", {"start": v(-53.34, -43.23) * mm, "end": v(-53.34, -43.81) * mm});
            skArc(sketch, "E349.0.22", {"start": v(-53.34, -43.81) * mm, "mid": v(-52.41, -46.06) * mm, "end": v(-50.17, -46.99) * mm});
            skLineSegment(sketch, "E349.0.23", {"start": v(-50.17, -46.99) * mm, "end": v(-28.58, -46.99) * mm});
            skArc(sketch, "E349.0.24", {"start": v(-28.58, -46.99) * mm, "mid": v(-26.33, -46.06) * mm, "end": v(-25.4, -43.81) * mm});
            skLineSegment(sketch, "E349.0.25", {"start": v(-25.4, -43.81) * mm, "end": v(-25.4, -34.92) * mm});
            skArc(sketch, "E349.0.26", {"start": v(-25.4, -34.92) * mm, "mid": v(-26.33, -32.68) * mm, "end": v(-28.58, -31.75) * mm});
            skLineSegment(sketch, "E349.0.27", {"start": v(-28.58, -31.75) * mm, "end": v(-31.43, -31.75) * mm});
            skArc(sketch, "E349.0.28", {"start": v(-31.43, -31.75) * mm, "mid": v(-41.15, -29.82) * mm, "end": v(-49.39, -24.31) * mm});
            skLineSegment(sketch, "E349.0.29", {"start": v(-49.39, -24.31) * mm, "end": v(-62.86, -10.84) * mm});
            skArc(sketch, "E349.0.30", {"start": v(-62.86, -10.84) * mm, "mid": v(-64.23, -3.92) * mm, "end": v(-58.37, 0) * mm});
            skLineSegment(sketch, "E349.0.31", {"start": v(-58.37, 0) * mm, "end": v(58.37, 0) * mm});
            skArc(sketch, "E349.0.32", {"start": v(62.86, -10.84) * mm, "mid": v(64.23, -3.92) * mm, "end": v(58.37, 0) * mm});
            skLineSegment(sketch, "E349.0.33", {"start": v(62.86, -10.84) * mm, "end": v(49.39, -24.31) * mm});
            skArc(sketch, "E349.0.34", {"start": v(31.43, -31.75) * mm, "mid": v(41.15, -29.82) * mm, "end": v(49.39, -24.31) * mm});
            skLineSegment(sketch, "E349.0.35", {"start": v(31.43, -31.75) * mm, "end": v(28.57, -31.75) * mm});
            skArc(sketch, "E349.0.36", {"start": v(28.57, -31.75) * mm, "mid": v(26.33, -32.68) * mm, "end": v(25.4, -34.92) * mm});
            skLineSegment(sketch, "E349.0.37", {"start": v(25.4, -34.92) * mm, "end": v(25.4, -43.81) * mm});
            skArc(sketch, "E349.0.38", {"start": v(25.4, -43.81) * mm, "mid": v(26.33, -46.06) * mm, "end": v(28.58, -46.99) * mm});
            skLineSegment(sketch, "E349.0.39", {"start": v(28.58, -46.99) * mm, "end": v(50.17, -46.99) * mm});
            skArc(sketch, "E349.0.40", {"start": v(50.17, -46.99) * mm, "mid": v(52.41, -46.06) * mm, "end": v(53.34, -43.81) * mm});
            skLineSegment(sketch, "E349.0.41", {"start": v(53.34, -43.81) * mm, "end": v(53.34, -43.23) * mm});
            skArc(sketch, "E349.0.42", {"start": v(54.27, -40.98) * mm, "mid": v(53.58, -42.01) * mm, "end": v(53.34, -43.23) * mm});
            skLineSegment(sketch, "E349.0.43", {"start": v(54.27, -40.98) * mm, "end": v(85.95, -9.3) * mm});
            skArc(sketch, "E350", {"start": v(39.37, -98.42) * mm, "mid": v(40.3, -100.67) * mm, "end": v(42.55, -101.6) * mm});
            skArc(sketch, "E351", {"start": v(-42.55, -101.6) * mm, "mid": v(-40.3, -100.67) * mm, "end": v(-39.37, -98.42) * mm});
            skSolve(sketch);
        }
        {
            var Q0;
            {var subQ0=sQuery(id+"F13.wireOp",EDGE,"E349.0.7");Q0=makeQuery(id+"F13.imprint","IMPRINT",FACE,{"disambiguationData":[TD([[makeQuery(id+"F13.imprint","IMPRINT",EDGE,{"derivedFrom":subQ0}),1.0]])]});}
            var Q1;
            Q1=makeQuery(id+"F13.imprint","IMPRINT",FACE,{"disambiguationData":[TD([[makeQuery(id+"F13.imprint","IMPRINT",EDGE,{"derivedFrom":sQuery(id+"F13.wireOp",EDGE,"E346.top")}),1.0]])]});
            extrude(context, id + "F14", {"entities" : qUnion([Q0, Q1]), "depth" : 6.35 * mm});
        }
        {
            var Q0;
            Q0=makeQuery(id+"F14.opExtrude","CAP_FACE",FACE,{"disambiguationData":[OSD([sQuery(id+"F13.wireOp",EDGE,"E346.bottom"),sQuery(id+"F13.wireOp",EDGE,"E346.top"),sQuery(id+"F13.wireOp",EDGE,"E346.left"),sQuery(id+"F13.wireOp",EDGE,"E346.right"),sQuery(id+"F13.wireOp",EDGE,"E347.bottom"),sQuery(id+"F13.wireOp",EDGE,"E347.left"),sQuery(id+"F13.wireOp",EDGE,"E347.right"),sQuery(id+"F13.wireOp",EDGE,"E348.trimOffspring")])],"isStart":false});
            var sketch = newSketch(context, id + "F15", { "sketchPlane" : qUnion([Q0])});
            skLineSegment(sketch, "E352.bottom", {"start": v(-225.43, -101.6) * mm, "end": v(-196.22, -101.6) * mm});
            skLineSegment(sketch, "E352.top", {"start": v(-225.43, -127) * mm, "end": v(225.43, -127) * mm});
            skLineSegment(sketch, "E352.left", {"start": v(-225.43, -101.6) * mm, "end": v(-225.43, -127) * mm});
            skLineSegment(sketch, "E352.right", {"start": v(225.43, -101.6) * mm, "end": v(225.43, -127) * mm});
            skLineSegment(sketch, "E353.left", {"start": v(-196.22, -101.6) * mm, "end": v(-196.22, -91.44) * mm});
            skLineSegment(sketch, "E353.right", {"start": v(196.22, -101.6) * mm, "end": v(196.22, -91.44) * mm});
            skLineSegment(sketch, "E354.top", {"start": v(-208.92, -91.44) * mm, "end": v(-196.22, -91.44) * mm});
            skLineSegment(sketch, "E354.left", {"start": v(-208.92, -54.61) * mm, "end": v(-208.92, -91.44) * mm});
            skLineSegment(sketch, "E355.top", {"start": v(196.22, -91.44) * mm, "end": v(208.92, -91.44) * mm});
            skLineSegment(sketch, "E355.right", {"start": v(208.92, -54.61) * mm, "end": v(208.92, -91.44) * mm});
            skLineSegment(sketch, "E356.bottom", {"start": v(149.86, -11.94) * mm, "end": v(167.64, -11.94) * mm});
            skLineSegment(sketch, "E356.left", {"start": v(149.86, -11.94) * mm, "end": v(149.86, -54.6) * mm});
            skLineSegment(sketch, "E356.right", {"start": v(167.64, -11.94) * mm, "end": v(167.64, -54.61) * mm});
            skLineSegment(sketch, "E357.bottom", {"start": v(-167.9, -11.94) * mm, "end": v(-150.11, -11.94) * mm});
            skLineSegment(sketch, "E357.left", {"start": v(-167.9, -11.94) * mm, "end": v(-167.9, -54.61) * mm});
            skLineSegment(sketch, "E357.right", {"start": v(-150.11, -11.94) * mm, "end": v(-150.11, -54.61) * mm});
            skLineSegment(sketch, "E358.trimOffspring", {"start": v(-150.11, -54.61) * mm, "end": v(149.86, -54.6) * mm});
            skLineSegment(sketch, "E359.trimOffspring", {"start": v(196.22, -101.6) * mm, "end": v(225.43, -101.6) * mm});
            skLineSegment(sketch, "E360", {"start": v(-208.92, -54.61) * mm, "end": v(-167.9, -54.61) * mm});
            skLineSegment(sketch, "E361", {"start": v(208.92, -54.61) * mm, "end": v(167.64, -54.61) * mm});
            skSolve(sketch);
        }
        {
            var Q0;
            Q0=qSketchRegion(id+"F15",true);
            extrude(context, id + "F16", {"entities" : qUnion([Q0]), "depth" : 6.35 * mm});
        }
    });
